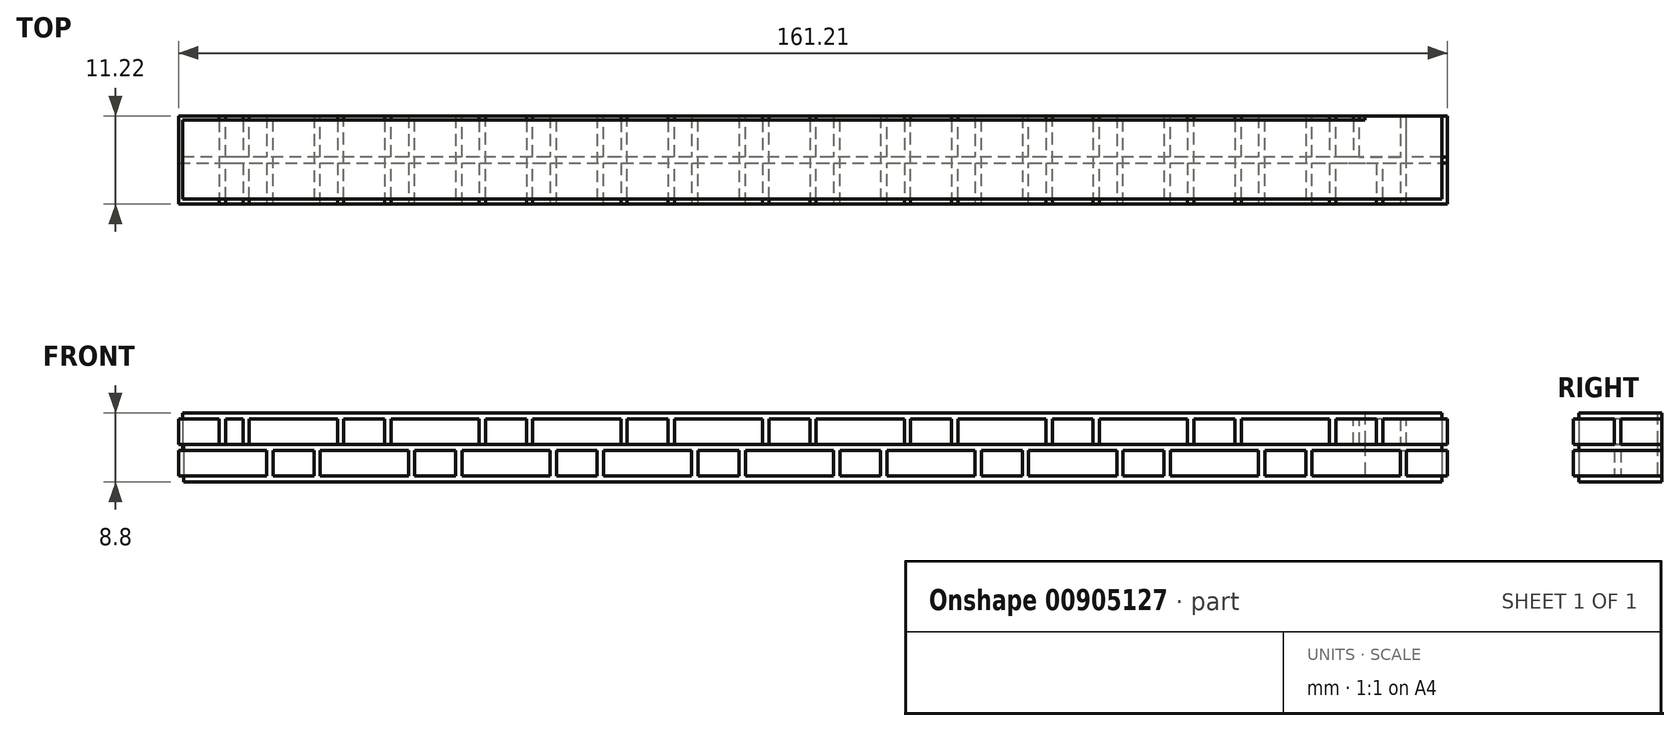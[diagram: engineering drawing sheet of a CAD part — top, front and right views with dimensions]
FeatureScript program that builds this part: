
annotation { "Feature Type Name" : "Feature", "Feature Type Description" : "" }
export const myFeature = defineFeature(function(context is Context, id is Id, definition is map)
    precondition{}
    {
        {
            var Q0;
            Q0=qCreatedBy(makeId("Top.planeOp"),FACE);
            var sketch = newSketch(context, id + "F0", { "sketchPlane" : qUnion([Q0])});
            skLineSegment(sketch, "E0", {"start": v(-80.6, -54.4) * mm, "end": v(-69.4, -54.4) * mm});
            skLineSegment(sketch, "E1", {"start": v(-69.4, -54.4) * mm, "end": v(-69.4, -59.6) * mm});
            skLineSegment(sketch, "E2", {"start": v(-69.4, -59.6) * mm, "end": v(-80.6, -59.6) * mm});
            skLineSegment(sketch, "E3", {"start": v(-80.6, -59.6) * mm, "end": v(-80.6, -54.4) * mm});
            skLineSegment(sketch, "E4", {"start": v(-68.6, -54.4) * mm, "end": v(-63.4, -54.4) * mm});
            skLineSegment(sketch, "E5", {"start": v(-63.4, -54.4) * mm, "end": v(-63.4, -65.6) * mm});
            skLineSegment(sketch, "E6", {"start": v(-63.4, -65.6) * mm, "end": v(-68.6, -65.6) * mm});
            skLineSegment(sketch, "E7", {"start": v(-68.6, -65.6) * mm, "end": v(-68.6, -54.4) * mm});
            skLineSegment(sketch, "E8", {"start": v(-80.6, -60.4) * mm, "end": v(-69.4, -60.4) * mm});
            skLineSegment(sketch, "E9", {"start": v(-69.4, -60.4) * mm, "end": v(-69.4, -65.6) * mm});
            skLineSegment(sketch, "E10", {"start": v(-69.4, -65.6) * mm, "end": v(-80.6, -65.6) * mm});
            skLineSegment(sketch, "E11", {"start": v(-80.6, -65.6) * mm, "end": v(-80.6, -60.4) * mm});
            skLineSegment(sketch, "E12", {"start": v(-62.6, -54.4) * mm, "end": v(-51.4, -54.4) * mm});
            skLineSegment(sketch, "E13", {"start": v(-51.4, -54.4) * mm, "end": v(-51.4, -59.6) * mm});
            skLineSegment(sketch, "E14", {"start": v(-51.4, -59.6) * mm, "end": v(-62.6, -59.6) * mm});
            skLineSegment(sketch, "E15", {"start": v(-62.6, -59.6) * mm, "end": v(-62.6, -54.4) * mm});
            skLineSegment(sketch, "E16", {"start": v(-50.6, -54.4) * mm, "end": v(-45.4, -54.4) * mm});
            skLineSegment(sketch, "E17", {"start": v(-45.4, -54.4) * mm, "end": v(-45.4, -65.6) * mm});
            skLineSegment(sketch, "E18", {"start": v(-45.4, -65.6) * mm, "end": v(-50.6, -65.6) * mm});
            skLineSegment(sketch, "E19", {"start": v(-50.6, -65.6) * mm, "end": v(-50.6, -54.4) * mm});
            skLineSegment(sketch, "E20", {"start": v(-62.6, -60.4) * mm, "end": v(-51.4, -60.4) * mm});
            skLineSegment(sketch, "E21", {"start": v(-51.4, -60.4) * mm, "end": v(-51.4, -65.6) * mm});
            skLineSegment(sketch, "E22", {"start": v(-51.4, -65.6) * mm, "end": v(-62.6, -65.6) * mm});
            skLineSegment(sketch, "E23", {"start": v(-62.6, -65.6) * mm, "end": v(-62.6, -60.4) * mm});
            skLineSegment(sketch, "E24", {"start": v(-44.6, -54.4) * mm, "end": v(-33.4, -54.4) * mm});
            skLineSegment(sketch, "E25", {"start": v(-33.4, -54.4) * mm, "end": v(-33.4, -59.6) * mm});
            skLineSegment(sketch, "E26", {"start": v(-33.4, -59.6) * mm, "end": v(-44.6, -59.6) * mm});
            skLineSegment(sketch, "E27", {"start": v(-44.6, -59.6) * mm, "end": v(-44.6, -54.4) * mm});
            skLineSegment(sketch, "E28", {"start": v(-32.6, -54.4) * mm, "end": v(-27.4, -54.4) * mm});
            skLineSegment(sketch, "E29", {"start": v(-27.4, -54.4) * mm, "end": v(-27.4, -65.6) * mm});
            skLineSegment(sketch, "E30", {"start": v(-27.4, -65.6) * mm, "end": v(-32.6, -65.6) * mm});
            skLineSegment(sketch, "E31", {"start": v(-32.6, -65.6) * mm, "end": v(-32.6, -54.4) * mm});
            skLineSegment(sketch, "E32", {"start": v(-44.6, -60.4) * mm, "end": v(-33.4, -60.4) * mm});
            skLineSegment(sketch, "E33", {"start": v(-33.4, -60.4) * mm, "end": v(-33.4, -65.6) * mm});
            skLineSegment(sketch, "E34", {"start": v(-33.4, -65.6) * mm, "end": v(-44.6, -65.6) * mm});
            skLineSegment(sketch, "E35", {"start": v(-44.6, -65.6) * mm, "end": v(-44.6, -60.4) * mm});
            skLineSegment(sketch, "E36", {"start": v(-26.6, -54.4) * mm, "end": v(-15.4, -54.4) * mm});
            skLineSegment(sketch, "E37", {"start": v(-15.4, -54.4) * mm, "end": v(-15.4, -59.6) * mm});
            skLineSegment(sketch, "E38", {"start": v(-15.4, -59.6) * mm, "end": v(-26.6, -59.6) * mm});
            skLineSegment(sketch, "E39", {"start": v(-26.6, -59.6) * mm, "end": v(-26.6, -54.4) * mm});
            skLineSegment(sketch, "E40", {"start": v(-14.6, -54.4) * mm, "end": v(-9.4, -54.4) * mm});
            skLineSegment(sketch, "E41", {"start": v(-9.4, -54.4) * mm, "end": v(-9.4, -65.6) * mm});
            skLineSegment(sketch, "E42", {"start": v(-9.4, -65.6) * mm, "end": v(-14.6, -65.6) * mm});
            skLineSegment(sketch, "E43", {"start": v(-14.6, -65.6) * mm, "end": v(-14.6, -54.4) * mm});
            skLineSegment(sketch, "E44", {"start": v(-26.6, -60.4) * mm, "end": v(-15.4, -60.4) * mm});
            skLineSegment(sketch, "E45", {"start": v(-15.4, -60.4) * mm, "end": v(-15.4, -65.6) * mm});
            skLineSegment(sketch, "E46", {"start": v(-15.4, -65.6) * mm, "end": v(-26.6, -65.6) * mm});
            skLineSegment(sketch, "E47", {"start": v(-26.6, -65.6) * mm, "end": v(-26.6, -60.4) * mm});
            skLineSegment(sketch, "E48", {"start": v(-8.6, -54.4) * mm, "end": v(2.6, -54.4) * mm});
            skLineSegment(sketch, "E49", {"start": v(2.6, -54.4) * mm, "end": v(2.6, -59.6) * mm});
            skLineSegment(sketch, "E50", {"start": v(2.6, -59.6) * mm, "end": v(-8.6, -59.6) * mm});
            skLineSegment(sketch, "E51", {"start": v(-8.6, -59.6) * mm, "end": v(-8.6, -54.4) * mm});
            skLineSegment(sketch, "E52", {"start": v(3.4, -54.4) * mm, "end": v(8.6, -54.4) * mm});
            skLineSegment(sketch, "E53", {"start": v(8.6, -54.4) * mm, "end": v(8.6, -65.6) * mm});
            skLineSegment(sketch, "E54", {"start": v(8.6, -65.6) * mm, "end": v(3.4, -65.6) * mm});
            skLineSegment(sketch, "E55", {"start": v(3.4, -65.6) * mm, "end": v(3.4, -54.4) * mm});
            skLineSegment(sketch, "E56", {"start": v(-8.6, -60.4) * mm, "end": v(2.6, -60.4) * mm});
            skLineSegment(sketch, "E57", {"start": v(2.6, -60.4) * mm, "end": v(2.6, -65.6) * mm});
            skLineSegment(sketch, "E58", {"start": v(2.6, -65.6) * mm, "end": v(-8.6, -65.6) * mm});
            skLineSegment(sketch, "E59", {"start": v(-8.6, -65.6) * mm, "end": v(-8.6, -60.4) * mm});
            skLineSegment(sketch, "E60", {"start": v(9.4, -54.4) * mm, "end": v(20.6, -54.4) * mm});
            skLineSegment(sketch, "E61", {"start": v(20.6, -54.4) * mm, "end": v(20.6, -59.6) * mm});
            skLineSegment(sketch, "E62", {"start": v(20.6, -59.6) * mm, "end": v(9.4, -59.6) * mm});
            skLineSegment(sketch, "E63", {"start": v(9.4, -59.6) * mm, "end": v(9.4, -54.4) * mm});
            skLineSegment(sketch, "E64", {"start": v(21.4, -54.4) * mm, "end": v(26.6, -54.4) * mm});
            skLineSegment(sketch, "E65", {"start": v(26.6, -54.4) * mm, "end": v(26.6, -65.6) * mm});
            skLineSegment(sketch, "E66", {"start": v(26.6, -65.6) * mm, "end": v(21.4, -65.6) * mm});
            skLineSegment(sketch, "E67", {"start": v(21.4, -65.6) * mm, "end": v(21.4, -54.4) * mm});
            skLineSegment(sketch, "E68", {"start": v(9.4, -60.4) * mm, "end": v(20.6, -60.4) * mm});
            skLineSegment(sketch, "E69", {"start": v(20.6, -60.4) * mm, "end": v(20.6, -65.6) * mm});
            skLineSegment(sketch, "E70", {"start": v(20.6, -65.6) * mm, "end": v(9.4, -65.6) * mm});
            skLineSegment(sketch, "E71", {"start": v(9.4, -65.6) * mm, "end": v(9.4, -60.4) * mm});
            skLineSegment(sketch, "E72", {"start": v(27.4, -54.4) * mm, "end": v(38.6, -54.4) * mm});
            skLineSegment(sketch, "E73", {"start": v(38.6, -54.4) * mm, "end": v(38.6, -59.6) * mm});
            skLineSegment(sketch, "E74", {"start": v(38.6, -59.6) * mm, "end": v(27.4, -59.6) * mm});
            skLineSegment(sketch, "E75", {"start": v(27.4, -59.6) * mm, "end": v(27.4, -54.4) * mm});
            skLineSegment(sketch, "E76", {"start": v(39.4, -54.4) * mm, "end": v(44.6, -54.4) * mm});
            skLineSegment(sketch, "E77", {"start": v(44.6, -54.4) * mm, "end": v(44.6, -65.6) * mm});
            skLineSegment(sketch, "E78", {"start": v(44.6, -65.6) * mm, "end": v(39.4, -65.6) * mm});
            skLineSegment(sketch, "E79", {"start": v(39.4, -65.6) * mm, "end": v(39.4, -54.4) * mm});
            skLineSegment(sketch, "E80", {"start": v(27.4, -60.4) * mm, "end": v(38.6, -60.4) * mm});
            skLineSegment(sketch, "E81", {"start": v(38.6, -60.4) * mm, "end": v(38.6, -65.6) * mm});
            skLineSegment(sketch, "E82", {"start": v(38.6, -65.6) * mm, "end": v(27.4, -65.6) * mm});
            skLineSegment(sketch, "E83", {"start": v(27.4, -65.6) * mm, "end": v(27.4, -60.4) * mm});
            skLineSegment(sketch, "E84", {"start": v(45.4, -54.4) * mm, "end": v(56.6, -54.4) * mm});
            skLineSegment(sketch, "E85", {"start": v(56.6, -54.4) * mm, "end": v(56.6, -59.6) * mm});
            skLineSegment(sketch, "E86", {"start": v(56.6, -59.6) * mm, "end": v(45.4, -59.6) * mm});
            skLineSegment(sketch, "E87", {"start": v(45.4, -59.6) * mm, "end": v(45.4, -54.4) * mm});
            skLineSegment(sketch, "E88", {"start": v(57.4, -54.4) * mm, "end": v(62.6, -54.4) * mm});
            skLineSegment(sketch, "E89", {"start": v(62.6, -54.4) * mm, "end": v(62.6, -65.6) * mm});
            skLineSegment(sketch, "E90", {"start": v(62.6, -65.6) * mm, "end": v(57.4, -65.6) * mm});
            skLineSegment(sketch, "E91", {"start": v(57.4, -65.6) * mm, "end": v(57.4, -54.4) * mm});
            skLineSegment(sketch, "E92", {"start": v(45.4, -60.4) * mm, "end": v(56.6, -60.4) * mm});
            skLineSegment(sketch, "E93", {"start": v(56.6, -60.4) * mm, "end": v(56.6, -65.6) * mm});
            skLineSegment(sketch, "E94", {"start": v(56.6, -65.6) * mm, "end": v(45.4, -65.6) * mm});
            skLineSegment(sketch, "E95", {"start": v(45.4, -65.6) * mm, "end": v(45.4, -60.4) * mm});
            skLineSegment(sketch, "E96", {"start": v(63.4, -54.4) * mm, "end": v(74.6, -54.4) * mm});
            skLineSegment(sketch, "E97", {"start": v(74.6, -54.4) * mm, "end": v(74.6, -59.6) * mm});
            skLineSegment(sketch, "E98", {"start": v(74.6, -59.6) * mm, "end": v(63.4, -59.6) * mm});
            skLineSegment(sketch, "E99", {"start": v(63.4, -59.6) * mm, "end": v(63.4, -54.4) * mm});
            skLineSegment(sketch, "E100", {"start": v(75.4, -54.4) * mm, "end": v(80.6, -54.4) * mm});
            skLineSegment(sketch, "E101", {"start": v(80.6, -54.4) * mm, "end": v(80.6, -65.6) * mm});
            skLineSegment(sketch, "E102", {"start": v(80.6, -65.6) * mm, "end": v(75.4, -65.6) * mm});
            skLineSegment(sketch, "E103", {"start": v(75.4, -65.6) * mm, "end": v(75.4, -54.4) * mm});
            skLineSegment(sketch, "E104", {"start": v(63.4, -60.4) * mm, "end": v(74.6, -60.4) * mm});
            skLineSegment(sketch, "E105", {"start": v(74.6, -60.4) * mm, "end": v(74.6, -65.6) * mm});
            skLineSegment(sketch, "E106", {"start": v(74.6, -65.6) * mm, "end": v(63.4, -65.6) * mm});
            skLineSegment(sketch, "E107", {"start": v(63.4, -65.6) * mm, "end": v(63.4, -60.4) * mm});
            skLineSegment(sketch, "E108", {"start": v(69.4, -53.6) * mm, "end": v(69.4, -42.4) * mm});
            skLineSegment(sketch, "E109", {"start": v(69.4, -42.4) * mm, "end": v(74.6, -42.4) * mm});
            skLineSegment(sketch, "E110", {"start": v(74.6, -42.4) * mm, "end": v(74.6, -53.6) * mm});
            skLineSegment(sketch, "E111", {"start": v(74.6, -53.6) * mm, "end": v(69.4, -53.6) * mm});
            skLineSegment(sketch, "E112", {"start": v(69.4, -41.6) * mm, "end": v(69.4, -36.4) * mm});
            skLineSegment(sketch, "E113", {"start": v(69.4, -36.4) * mm, "end": v(80.6, -36.4) * mm});
            skLineSegment(sketch, "E114", {"start": v(80.6, -36.4) * mm, "end": v(80.6, -41.6) * mm});
            skLineSegment(sketch, "E115", {"start": v(80.6, -41.6) * mm, "end": v(69.4, -41.6) * mm});
            skLineSegment(sketch, "E116", {"start": v(75.4, -53.6) * mm, "end": v(75.4, -42.4) * mm});
            skLineSegment(sketch, "E117", {"start": v(75.4, -42.4) * mm, "end": v(80.6, -42.4) * mm});
            skLineSegment(sketch, "E118", {"start": v(80.6, -42.4) * mm, "end": v(80.6, -53.6) * mm});
            skLineSegment(sketch, "E119", {"start": v(80.6, -53.6) * mm, "end": v(75.4, -53.6) * mm});
            skLineSegment(sketch, "E120", {"start": v(69.4, -35.6) * mm, "end": v(69.4, -24.4) * mm});
            skLineSegment(sketch, "E121", {"start": v(69.4, -24.4) * mm, "end": v(74.6, -24.4) * mm});
            skLineSegment(sketch, "E122", {"start": v(74.6, -24.4) * mm, "end": v(74.6, -35.6) * mm});
            skLineSegment(sketch, "E123", {"start": v(74.6, -35.6) * mm, "end": v(69.4, -35.6) * mm});
            skLineSegment(sketch, "E124", {"start": v(69.4, -23.6) * mm, "end": v(69.4, -18.4) * mm});
            skLineSegment(sketch, "E125", {"start": v(69.4, -18.4) * mm, "end": v(80.6, -18.4) * mm});
            skLineSegment(sketch, "E126", {"start": v(80.6, -18.4) * mm, "end": v(80.6, -23.6) * mm});
            skLineSegment(sketch, "E127", {"start": v(80.6, -23.6) * mm, "end": v(69.4, -23.6) * mm});
            skLineSegment(sketch, "E128", {"start": v(75.4, -35.6) * mm, "end": v(75.4, -24.4) * mm});
            skLineSegment(sketch, "E129", {"start": v(75.4, -24.4) * mm, "end": v(80.6, -24.4) * mm});
            skLineSegment(sketch, "E130", {"start": v(80.6, -24.4) * mm, "end": v(80.6, -35.6) * mm});
            skLineSegment(sketch, "E131", {"start": v(80.6, -35.6) * mm, "end": v(75.4, -35.6) * mm});
            skLineSegment(sketch, "E132", {"start": v(69.4, -17.6) * mm, "end": v(69.4, -6.4) * mm});
            skLineSegment(sketch, "E133", {"start": v(69.4, -6.4) * mm, "end": v(74.6, -6.4) * mm});
            skLineSegment(sketch, "E134", {"start": v(74.6, -6.4) * mm, "end": v(74.6, -17.6) * mm});
            skLineSegment(sketch, "E135", {"start": v(74.6, -17.6) * mm, "end": v(69.4, -17.6) * mm});
            skLineSegment(sketch, "E136", {"start": v(69.4, -5.6) * mm, "end": v(69.4, -0.4) * mm});
            skLineSegment(sketch, "E137", {"start": v(69.4, -0.4) * mm, "end": v(80.6, -0.4) * mm});
            skLineSegment(sketch, "E138", {"start": v(80.6, -0.4) * mm, "end": v(80.6, -5.6) * mm});
            skLineSegment(sketch, "E139", {"start": v(80.6, -5.6) * mm, "end": v(69.4, -5.6) * mm});
            skLineSegment(sketch, "E140", {"start": v(75.4, -17.6) * mm, "end": v(75.4, -6.4) * mm});
            skLineSegment(sketch, "E141", {"start": v(75.4, -6.4) * mm, "end": v(80.6, -6.4) * mm});
            skLineSegment(sketch, "E142", {"start": v(80.6, -6.4) * mm, "end": v(80.6, -17.6) * mm});
            skLineSegment(sketch, "E143", {"start": v(80.6, -17.6) * mm, "end": v(75.4, -17.6) * mm});
            skLineSegment(sketch, "E144", {"start": v(69.4, 0.4) * mm, "end": v(69.4, 11.6) * mm});
            skLineSegment(sketch, "E145", {"start": v(69.4, 11.6) * mm, "end": v(74.6, 11.6) * mm});
            skLineSegment(sketch, "E146", {"start": v(74.6, 11.6) * mm, "end": v(74.6, 0.4) * mm});
            skLineSegment(sketch, "E147", {"start": v(74.6, 0.4) * mm, "end": v(69.4, 0.4) * mm});
            skLineSegment(sketch, "E148", {"start": v(69.4, 12.4) * mm, "end": v(69.4, 17.6) * mm});
            skLineSegment(sketch, "E149", {"start": v(69.4, 17.6) * mm, "end": v(80.6, 17.6) * mm});
            skLineSegment(sketch, "E150", {"start": v(80.6, 17.6) * mm, "end": v(80.6, 12.4) * mm});
            skLineSegment(sketch, "E151", {"start": v(80.6, 12.4) * mm, "end": v(69.4, 12.4) * mm});
            skLineSegment(sketch, "E152", {"start": v(75.4, 0.4) * mm, "end": v(75.4, 11.6) * mm});
            skLineSegment(sketch, "E153", {"start": v(75.4, 11.6) * mm, "end": v(80.6, 11.6) * mm});
            skLineSegment(sketch, "E154", {"start": v(80.6, 11.6) * mm, "end": v(80.6, 0.4) * mm});
            skLineSegment(sketch, "E155", {"start": v(80.6, 0.4) * mm, "end": v(75.4, 0.4) * mm});
            skLineSegment(sketch, "E156", {"start": v(69.4, 18.4) * mm, "end": v(69.4, 29.6) * mm});
            skLineSegment(sketch, "E157", {"start": v(69.4, 29.6) * mm, "end": v(74.6, 29.6) * mm});
            skLineSegment(sketch, "E158", {"start": v(74.6, 29.6) * mm, "end": v(74.6, 18.4) * mm});
            skLineSegment(sketch, "E159", {"start": v(74.6, 18.4) * mm, "end": v(69.4, 18.4) * mm});
            skLineSegment(sketch, "E160", {"start": v(69.4, 30.4) * mm, "end": v(69.4, 35.6) * mm});
            skLineSegment(sketch, "E161", {"start": v(69.4, 35.6) * mm, "end": v(80.6, 35.6) * mm});
            skLineSegment(sketch, "E162", {"start": v(80.6, 35.6) * mm, "end": v(80.6, 30.4) * mm});
            skLineSegment(sketch, "E163", {"start": v(80.6, 30.4) * mm, "end": v(69.4, 30.4) * mm});
            skLineSegment(sketch, "E164", {"start": v(75.4, 18.4) * mm, "end": v(75.4, 29.6) * mm});
            skLineSegment(sketch, "E165", {"start": v(75.4, 29.6) * mm, "end": v(80.6, 29.6) * mm});
            skLineSegment(sketch, "E166", {"start": v(80.6, 29.6) * mm, "end": v(80.6, 18.4) * mm});
            skLineSegment(sketch, "E167", {"start": v(80.6, 18.4) * mm, "end": v(75.4, 18.4) * mm});
            skLineSegment(sketch, "E168", {"start": v(69.4, 36.4) * mm, "end": v(69.4, 47.6) * mm});
            skLineSegment(sketch, "E169", {"start": v(69.4, 47.6) * mm, "end": v(74.6, 47.6) * mm});
            skLineSegment(sketch, "E170", {"start": v(74.6, 47.6) * mm, "end": v(74.6, 36.4) * mm});
            skLineSegment(sketch, "E171", {"start": v(74.6, 36.4) * mm, "end": v(69.4, 36.4) * mm});
            skLineSegment(sketch, "E172", {"start": v(69.4, 48.4) * mm, "end": v(69.4, 53.6) * mm});
            skLineSegment(sketch, "E173", {"start": v(69.4, 53.6) * mm, "end": v(80.6, 53.6) * mm});
            skLineSegment(sketch, "E174", {"start": v(80.6, 53.6) * mm, "end": v(80.6, 48.4) * mm});
            skLineSegment(sketch, "E175", {"start": v(80.6, 48.4) * mm, "end": v(69.4, 48.4) * mm});
            skLineSegment(sketch, "E176", {"start": v(75.4, 36.4) * mm, "end": v(75.4, 47.6) * mm});
            skLineSegment(sketch, "E177", {"start": v(75.4, 47.6) * mm, "end": v(80.6, 47.6) * mm});
            skLineSegment(sketch, "E178", {"start": v(80.6, 47.6) * mm, "end": v(80.6, 36.4) * mm});
            skLineSegment(sketch, "E179", {"start": v(80.6, 36.4) * mm, "end": v(75.4, 36.4) * mm});
            skLineSegment(sketch, "E180", {"start": v(75.4, 54.4) * mm, "end": v(75.4, 65.6) * mm});
            skLineSegment(sketch, "E181", {"start": v(75.4, 65.6) * mm, "end": v(80.6, 65.6) * mm});
            skLineSegment(sketch, "E182", {"start": v(80.6, 65.6) * mm, "end": v(80.6, 54.4) * mm});
            skLineSegment(sketch, "E183", {"start": v(80.6, 54.4) * mm, "end": v(75.4, 54.4) * mm});
            skLineSegment(sketch, "E184", {"start": v(-80.6, 65.6) * mm, "end": v(-69.4, 65.6) * mm});
            skLineSegment(sketch, "E185", {"start": v(-69.4, 65.6) * mm, "end": v(-69.4, 60.4) * mm});
            skLineSegment(sketch, "E186", {"start": v(-69.4, 60.4) * mm, "end": v(-80.6, 60.4) * mm});
            skLineSegment(sketch, "E187", {"start": v(-80.6, 60.4) * mm, "end": v(-80.6, 65.6) * mm});
            skLineSegment(sketch, "E188", {"start": v(-68.6, 65.6) * mm, "end": v(-63.4, 65.6) * mm});
            skLineSegment(sketch, "E189", {"start": v(-63.4, 65.6) * mm, "end": v(-63.4, 54.4) * mm});
            skLineSegment(sketch, "E190", {"start": v(-63.4, 54.4) * mm, "end": v(-68.6, 54.4) * mm});
            skLineSegment(sketch, "E191", {"start": v(-68.6, 54.4) * mm, "end": v(-68.6, 65.6) * mm});
            skLineSegment(sketch, "E192", {"start": v(-80.6, 59.6) * mm, "end": v(-69.4, 59.6) * mm});
            skLineSegment(sketch, "E193", {"start": v(-69.4, 59.6) * mm, "end": v(-69.4, 54.4) * mm});
            skLineSegment(sketch, "E194", {"start": v(-69.4, 54.4) * mm, "end": v(-80.6, 54.4) * mm});
            skLineSegment(sketch, "E195", {"start": v(-80.6, 54.4) * mm, "end": v(-80.6, 59.6) * mm});
            skLineSegment(sketch, "E196", {"start": v(-62.6, 65.6) * mm, "end": v(-51.4, 65.6) * mm});
            skLineSegment(sketch, "E197", {"start": v(-51.4, 65.6) * mm, "end": v(-51.4, 60.4) * mm});
            skLineSegment(sketch, "E198", {"start": v(-51.4, 60.4) * mm, "end": v(-62.6, 60.4) * mm});
            skLineSegment(sketch, "E199", {"start": v(-62.6, 60.4) * mm, "end": v(-62.6, 65.6) * mm});
            skLineSegment(sketch, "E200", {"start": v(-50.6, 65.6) * mm, "end": v(-45.4, 65.6) * mm});
            skLineSegment(sketch, "E201", {"start": v(-45.4, 65.6) * mm, "end": v(-45.4, 54.4) * mm});
            skLineSegment(sketch, "E202", {"start": v(-45.4, 54.4) * mm, "end": v(-50.6, 54.4) * mm});
            skLineSegment(sketch, "E203", {"start": v(-50.6, 54.4) * mm, "end": v(-50.6, 65.6) * mm});
            skLineSegment(sketch, "E204", {"start": v(-62.6, 59.6) * mm, "end": v(-51.4, 59.6) * mm});
            skLineSegment(sketch, "E205", {"start": v(-51.4, 59.6) * mm, "end": v(-51.4, 54.4) * mm});
            skLineSegment(sketch, "E206", {"start": v(-51.4, 54.4) * mm, "end": v(-62.6, 54.4) * mm});
            skLineSegment(sketch, "E207", {"start": v(-62.6, 54.4) * mm, "end": v(-62.6, 59.6) * mm});
            skLineSegment(sketch, "E208", {"start": v(-44.6, 65.6) * mm, "end": v(-33.4, 65.6) * mm});
            skLineSegment(sketch, "E209", {"start": v(-33.4, 65.6) * mm, "end": v(-33.4, 60.4) * mm});
            skLineSegment(sketch, "E210", {"start": v(-33.4, 60.4) * mm, "end": v(-44.6, 60.4) * mm});
            skLineSegment(sketch, "E211", {"start": v(-44.6, 60.4) * mm, "end": v(-44.6, 65.6) * mm});
            skLineSegment(sketch, "E212", {"start": v(-32.6, 65.6) * mm, "end": v(-27.4, 65.6) * mm});
            skLineSegment(sketch, "E213", {"start": v(-27.4, 65.6) * mm, "end": v(-27.4, 54.4) * mm});
            skLineSegment(sketch, "E214", {"start": v(-27.4, 54.4) * mm, "end": v(-32.6, 54.4) * mm});
            skLineSegment(sketch, "E215", {"start": v(-32.6, 54.4) * mm, "end": v(-32.6, 65.6) * mm});
            skLineSegment(sketch, "E216", {"start": v(-44.6, 59.6) * mm, "end": v(-33.4, 59.6) * mm});
            skLineSegment(sketch, "E217", {"start": v(-33.4, 59.6) * mm, "end": v(-33.4, 54.4) * mm});
            skLineSegment(sketch, "E218", {"start": v(-33.4, 54.4) * mm, "end": v(-44.6, 54.4) * mm});
            skLineSegment(sketch, "E219", {"start": v(-44.6, 54.4) * mm, "end": v(-44.6, 59.6) * mm});
            skLineSegment(sketch, "E220", {"start": v(-26.6, 65.6) * mm, "end": v(-15.4, 65.6) * mm});
            skLineSegment(sketch, "E221", {"start": v(-15.4, 65.6) * mm, "end": v(-15.4, 60.4) * mm});
            skLineSegment(sketch, "E222", {"start": v(-15.4, 60.4) * mm, "end": v(-26.6, 60.4) * mm});
            skLineSegment(sketch, "E223", {"start": v(-26.6, 60.4) * mm, "end": v(-26.6, 65.6) * mm});
            skLineSegment(sketch, "E224", {"start": v(-14.6, 65.6) * mm, "end": v(-9.4, 65.6) * mm});
            skLineSegment(sketch, "E225", {"start": v(-9.4, 65.6) * mm, "end": v(-9.4, 54.4) * mm});
            skLineSegment(sketch, "E226", {"start": v(-9.4, 54.4) * mm, "end": v(-14.6, 54.4) * mm});
            skLineSegment(sketch, "E227", {"start": v(-14.6, 54.4) * mm, "end": v(-14.6, 65.6) * mm});
            skLineSegment(sketch, "E228", {"start": v(-26.6, 59.6) * mm, "end": v(-15.4, 59.6) * mm});
            skLineSegment(sketch, "E229", {"start": v(-15.4, 59.6) * mm, "end": v(-15.4, 54.4) * mm});
            skLineSegment(sketch, "E230", {"start": v(-15.4, 54.4) * mm, "end": v(-26.6, 54.4) * mm});
            skLineSegment(sketch, "E231", {"start": v(-26.6, 54.4) * mm, "end": v(-26.6, 59.6) * mm});
            skLineSegment(sketch, "E232", {"start": v(-8.6, 65.6) * mm, "end": v(2.6, 65.6) * mm});
            skLineSegment(sketch, "E233", {"start": v(2.6, 65.6) * mm, "end": v(2.6, 60.4) * mm});
            skLineSegment(sketch, "E234", {"start": v(2.6, 60.4) * mm, "end": v(-8.6, 60.4) * mm});
            skLineSegment(sketch, "E235", {"start": v(-8.6, 60.4) * mm, "end": v(-8.6, 65.6) * mm});
            skLineSegment(sketch, "E236", {"start": v(3.4, 65.6) * mm, "end": v(8.6, 65.6) * mm});
            skLineSegment(sketch, "E237", {"start": v(8.6, 65.6) * mm, "end": v(8.6, 54.4) * mm});
            skLineSegment(sketch, "E238", {"start": v(8.6, 54.4) * mm, "end": v(3.4, 54.4) * mm});
            skLineSegment(sketch, "E239", {"start": v(3.4, 54.4) * mm, "end": v(3.4, 65.6) * mm});
            skLineSegment(sketch, "E240", {"start": v(-8.6, 59.6) * mm, "end": v(2.6, 59.6) * mm});
            skLineSegment(sketch, "E241", {"start": v(2.6, 59.6) * mm, "end": v(2.6, 54.4) * mm});
            skLineSegment(sketch, "E242", {"start": v(2.6, 54.4) * mm, "end": v(-8.6, 54.4) * mm});
            skLineSegment(sketch, "E243", {"start": v(-8.6, 54.4) * mm, "end": v(-8.6, 59.6) * mm});
            skLineSegment(sketch, "E244", {"start": v(9.4, 65.6) * mm, "end": v(20.6, 65.6) * mm});
            skLineSegment(sketch, "E245", {"start": v(20.6, 65.6) * mm, "end": v(20.6, 60.4) * mm});
            skLineSegment(sketch, "E246", {"start": v(20.6, 60.4) * mm, "end": v(9.4, 60.4) * mm});
            skLineSegment(sketch, "E247", {"start": v(9.4, 60.4) * mm, "end": v(9.4, 65.6) * mm});
            skLineSegment(sketch, "E248", {"start": v(21.4, 65.6) * mm, "end": v(26.6, 65.6) * mm});
            skLineSegment(sketch, "E249", {"start": v(26.6, 65.6) * mm, "end": v(26.6, 54.4) * mm});
            skLineSegment(sketch, "E250", {"start": v(26.6, 54.4) * mm, "end": v(21.4, 54.4) * mm});
            skLineSegment(sketch, "E251", {"start": v(21.4, 54.4) * mm, "end": v(21.4, 65.6) * mm});
            skLineSegment(sketch, "E252", {"start": v(9.4, 59.6) * mm, "end": v(20.6, 59.6) * mm});
            skLineSegment(sketch, "E253", {"start": v(20.6, 59.6) * mm, "end": v(20.6, 54.4) * mm});
            skLineSegment(sketch, "E254", {"start": v(20.6, 54.4) * mm, "end": v(9.4, 54.4) * mm});
            skLineSegment(sketch, "E255", {"start": v(9.4, 54.4) * mm, "end": v(9.4, 59.6) * mm});
            skLineSegment(sketch, "E256", {"start": v(27.4, 65.6) * mm, "end": v(38.6, 65.6) * mm});
            skLineSegment(sketch, "E257", {"start": v(38.6, 65.6) * mm, "end": v(38.6, 60.4) * mm});
            skLineSegment(sketch, "E258", {"start": v(38.6, 60.4) * mm, "end": v(27.4, 60.4) * mm});
            skLineSegment(sketch, "E259", {"start": v(27.4, 60.4) * mm, "end": v(27.4, 65.6) * mm});
            skLineSegment(sketch, "E260", {"start": v(39.4, 65.6) * mm, "end": v(44.6, 65.6) * mm});
            skLineSegment(sketch, "E261", {"start": v(44.6, 65.6) * mm, "end": v(44.6, 54.4) * mm});
            skLineSegment(sketch, "E262", {"start": v(44.6, 54.4) * mm, "end": v(39.4, 54.4) * mm});
            skLineSegment(sketch, "E263", {"start": v(39.4, 54.4) * mm, "end": v(39.4, 65.6) * mm});
            skLineSegment(sketch, "E264", {"start": v(27.4, 59.6) * mm, "end": v(38.6, 59.6) * mm});
            skLineSegment(sketch, "E265", {"start": v(38.6, 59.6) * mm, "end": v(38.6, 54.4) * mm});
            skLineSegment(sketch, "E266", {"start": v(38.6, 54.4) * mm, "end": v(27.4, 54.4) * mm});
            skLineSegment(sketch, "E267", {"start": v(27.4, 54.4) * mm, "end": v(27.4, 59.6) * mm});
            skLineSegment(sketch, "E268", {"start": v(45.4, 65.6) * mm, "end": v(56.6, 65.6) * mm});
            skLineSegment(sketch, "E269", {"start": v(56.6, 65.6) * mm, "end": v(56.6, 60.4) * mm});
            skLineSegment(sketch, "E270", {"start": v(56.6, 60.4) * mm, "end": v(45.4, 60.4) * mm});
            skLineSegment(sketch, "E271", {"start": v(45.4, 60.4) * mm, "end": v(45.4, 65.6) * mm});
            skLineSegment(sketch, "E272", {"start": v(57.4, 65.6) * mm, "end": v(62.6, 65.6) * mm});
            skLineSegment(sketch, "E273", {"start": v(62.6, 65.6) * mm, "end": v(62.6, 54.4) * mm});
            skLineSegment(sketch, "E274", {"start": v(62.6, 54.4) * mm, "end": v(57.4, 54.4) * mm});
            skLineSegment(sketch, "E275", {"start": v(57.4, 54.4) * mm, "end": v(57.4, 65.6) * mm});
            skLineSegment(sketch, "E276", {"start": v(45.4, 59.6) * mm, "end": v(56.6, 59.6) * mm});
            skLineSegment(sketch, "E277", {"start": v(56.6, 59.6) * mm, "end": v(56.6, 54.4) * mm});
            skLineSegment(sketch, "E278", {"start": v(56.6, 54.4) * mm, "end": v(45.4, 54.4) * mm});
            skLineSegment(sketch, "E279", {"start": v(45.4, 54.4) * mm, "end": v(45.4, 59.6) * mm});
            skLineSegment(sketch, "E280", {"start": v(63.4, 65.6) * mm, "end": v(74.6, 65.6) * mm});
            skLineSegment(sketch, "E281", {"start": v(74.6, 65.6) * mm, "end": v(74.6, 60.4) * mm});
            skLineSegment(sketch, "E282", {"start": v(74.6, 60.4) * mm, "end": v(63.4, 60.4) * mm});
            skLineSegment(sketch, "E283", {"start": v(63.4, 60.4) * mm, "end": v(63.4, 65.6) * mm});
            skLineSegment(sketch, "E284", {"start": v(63.4, 59.6) * mm, "end": v(74.6, 59.6) * mm});
            skLineSegment(sketch, "E285", {"start": v(74.6, 59.6) * mm, "end": v(74.6, 54.4) * mm});
            skLineSegment(sketch, "E286", {"start": v(74.6, 54.4) * mm, "end": v(63.4, 54.4) * mm});
            skLineSegment(sketch, "E287", {"start": v(63.4, 54.4) * mm, "end": v(63.4, 59.6) * mm});
            skSolve(sketch);
        }
        {
            var Q0;
            Q0=makeQuery(id+"F0.imprint","IMPRINT",FACE,{"disambiguationData":[TD([[makeQuery(id+"F0.imprint","IMPRINT",EDGE,{"derivedFrom":sQuery(id+"F0.wireOp",EDGE,"E244")}),-1.0]])]});
            var Q1;
            Q1=makeQuery(id+"F0.imprint","IMPRINT",FACE,{"disambiguationData":[TD([[makeQuery(id+"F0.imprint","IMPRINT",EDGE,{"derivedFrom":sQuery(id+"F0.wireOp",EDGE,"E180")}),-1.0]])]});
            var Q2;
            Q2=makeQuery(id+"F0.imprint","IMPRINT",FACE,{"disambiguationData":[TD([[makeQuery(id+"F0.imprint","IMPRINT",EDGE,{"derivedFrom":sQuery(id+"F0.wireOp",EDGE,"E204")}),-1.0]])]});
            var Q3;
            Q3=makeQuery(id+"F0.imprint","IMPRINT",FACE,{"disambiguationData":[TD([[makeQuery(id+"F0.imprint","IMPRINT",EDGE,{"derivedFrom":sQuery(id+"F0.wireOp",EDGE,"E140")}),-1.0]])]});
            var Q4;
            Q4=makeQuery(id+"F0.imprint","IMPRINT",FACE,{"disambiguationData":[TD([[makeQuery(id+"F0.imprint","IMPRINT",EDGE,{"derivedFrom":sQuery(id+"F0.wireOp",EDGE,"E164")}),-1.0]])]});
            var Q5;
            Q5=makeQuery(id+"F0.imprint","IMPRINT",FACE,{"disambiguationData":[TD([[makeQuery(id+"F0.imprint","IMPRINT",EDGE,{"derivedFrom":sQuery(id+"F0.wireOp",EDGE,"E168")}),-1.0]])]});
            var Q6;
            Q6=makeQuery(id+"F0.imprint","IMPRINT",FACE,{"disambiguationData":[TD([[makeQuery(id+"F0.imprint","IMPRINT",EDGE,{"derivedFrom":sQuery(id+"F0.wireOp",EDGE,"E176")}),-1.0]])]});
            var Q7;
            Q7=makeQuery(id+"F0.imprint","IMPRINT",FACE,{"disambiguationData":[TD([[makeQuery(id+"F0.imprint","IMPRINT",EDGE,{"derivedFrom":sQuery(id+"F0.wireOp",EDGE,"E156")}),-1.0]])]});
            var Q8;
            Q8=makeQuery(id+"F0.imprint","IMPRINT",FACE,{"disambiguationData":[TD([[makeQuery(id+"F0.imprint","IMPRINT",EDGE,{"derivedFrom":sQuery(id+"F0.wireOp",EDGE,"E32")}),-1.0]])]});
            var Q9;
            Q9=makeQuery(id+"F0.imprint","IMPRINT",FACE,{"disambiguationData":[TD([[makeQuery(id+"F0.imprint","IMPRINT",EDGE,{"derivedFrom":sQuery(id+"F0.wireOp",EDGE,"E220")}),-1.0]])]});
            var Q10;
            Q10=makeQuery(id+"F0.imprint","IMPRINT",FACE,{"disambiguationData":[TD([[makeQuery(id+"F0.imprint","IMPRINT",EDGE,{"derivedFrom":sQuery(id+"F0.wireOp",EDGE,"E60")}),-1.0]])]});
            var Q11;
            Q11=makeQuery(id+"F0.imprint","IMPRINT",FACE,{"disambiguationData":[TD([[makeQuery(id+"F0.imprint","IMPRINT",EDGE,{"derivedFrom":sQuery(id+"F0.wireOp",EDGE,"E152")}),-1.0]])]});
            var Q12;
            Q12=makeQuery(id+"F0.imprint","IMPRINT",FACE,{"disambiguationData":[TD([[makeQuery(id+"F0.imprint","IMPRINT",EDGE,{"derivedFrom":sQuery(id+"F0.wireOp",EDGE,"E252")}),-1.0]])]});
            var Q13;
            Q13=makeQuery(id+"F0.imprint","IMPRINT",FACE,{"disambiguationData":[TD([[makeQuery(id+"F0.imprint","IMPRINT",EDGE,{"derivedFrom":sQuery(id+"F0.wireOp",EDGE,"E280")}),-1.0]])]});
            var Q14;
            Q14=makeQuery(id+"F0.imprint","IMPRINT",FACE,{"disambiguationData":[TD([[makeQuery(id+"F0.imprint","IMPRINT",EDGE,{"derivedFrom":sQuery(id+"F0.wireOp",EDGE,"E44")}),-1.0]])]});
            var Q15;
            Q15=makeQuery(id+"F0.imprint","IMPRINT",FACE,{"disambiguationData":[TD([[makeQuery(id+"F0.imprint","IMPRINT",EDGE,{"derivedFrom":sQuery(id+"F0.wireOp",EDGE,"E128")}),-1.0]])]});
            var Q16;
            Q16=makeQuery(id+"F0.imprint","IMPRINT",FACE,{"disambiguationData":[TD([[makeQuery(id+"F0.imprint","IMPRINT",EDGE,{"derivedFrom":sQuery(id+"F0.wireOp",EDGE,"E216")}),-1.0]])]});
            var Q17;
            Q17=makeQuery(id+"F0.imprint","IMPRINT",FACE,{"disambiguationData":[TD([[makeQuery(id+"F0.imprint","IMPRINT",EDGE,{"derivedFrom":sQuery(id+"F0.wireOp",EDGE,"E284")}),-1.0]])]});
            var Q18;
            Q18=makeQuery(id+"F0.imprint","IMPRINT",FACE,{"disambiguationData":[TD([[makeQuery(id+"F0.imprint","IMPRINT",EDGE,{"derivedFrom":sQuery(id+"F0.wireOp",EDGE,"E268")}),-1.0]])]});
            var Q19;
            Q19=makeQuery(id+"F0.imprint","IMPRINT",FACE,{"disambiguationData":[TD([[makeQuery(id+"F0.imprint","IMPRINT",EDGE,{"derivedFrom":sQuery(id+"F0.wireOp",EDGE,"E208")}),-1.0]])]});
            var Q20;
            Q20=makeQuery(id+"F0.imprint","IMPRINT",FACE,{"disambiguationData":[TD([[makeQuery(id+"F0.imprint","IMPRINT",EDGE,{"derivedFrom":sQuery(id+"F0.wireOp",EDGE,"E8")}),-1.0]])]});
            var Q21;
            Q21=makeQuery(id+"F0.imprint","IMPRINT",FACE,{"disambiguationData":[TD([[makeQuery(id+"F0.imprint","IMPRINT",EDGE,{"derivedFrom":sQuery(id+"F0.wireOp",EDGE,"E104")}),-1.0]])]});
            var Q22;
            Q22=makeQuery(id+"F0.imprint","IMPRINT",FACE,{"disambiguationData":[TD([[makeQuery(id+"F0.imprint","IMPRINT",EDGE,{"derivedFrom":sQuery(id+"F0.wireOp",EDGE,"E196")}),-1.0]])]});
            var Q23;
            Q23=makeQuery(id+"F0.imprint","IMPRINT",FACE,{"disambiguationData":[TD([[makeQuery(id+"F0.imprint","IMPRINT",EDGE,{"derivedFrom":sQuery(id+"F0.wireOp",EDGE,"E232")}),-1.0]])]});
            var Q24;
            Q24=makeQuery(id+"F0.imprint","IMPRINT",FACE,{"disambiguationData":[TD([[makeQuery(id+"F0.imprint","IMPRINT",EDGE,{"derivedFrom":sQuery(id+"F0.wireOp",EDGE,"E92")}),-1.0]])]});
            var Q25;
            Q25=makeQuery(id+"F0.imprint","IMPRINT",FACE,{"disambiguationData":[TD([[makeQuery(id+"F0.imprint","IMPRINT",EDGE,{"derivedFrom":sQuery(id+"F0.wireOp",EDGE,"E24")}),-1.0]])]});
            var Q26;
            Q26=makeQuery(id+"F0.imprint","IMPRINT",FACE,{"disambiguationData":[TD([[makeQuery(id+"F0.imprint","IMPRINT",EDGE,{"derivedFrom":sQuery(id+"F0.wireOp",EDGE,"E228")}),-1.0]])]});
            var Q27;
            Q27=makeQuery(id+"F0.imprint","IMPRINT",FACE,{"disambiguationData":[TD([[makeQuery(id+"F0.imprint","IMPRINT",EDGE,{"derivedFrom":sQuery(id+"F0.wireOp",EDGE,"E256")}),-1.0]])]});
            var Q28;
            Q28=makeQuery(id+"F0.imprint","IMPRINT",FACE,{"disambiguationData":[TD([[makeQuery(id+"F0.imprint","IMPRINT",EDGE,{"derivedFrom":sQuery(id+"F0.wireOp",EDGE,"E276")}),-1.0]])]});
            var Q29;
            Q29=makeQuery(id+"F0.imprint","IMPRINT",FACE,{"disambiguationData":[TD([[makeQuery(id+"F0.imprint","IMPRINT",EDGE,{"derivedFrom":sQuery(id+"F0.wireOp",EDGE,"E68")}),-1.0]])]});
            var Q30;
            Q30=makeQuery(id+"F0.imprint","IMPRINT",FACE,{"disambiguationData":[TD([[makeQuery(id+"F0.imprint","IMPRINT",EDGE,{"derivedFrom":sQuery(id+"F0.wireOp",EDGE,"E36")}),-1.0]])]});
            var Q31;
            Q31=makeQuery(id+"F0.imprint","IMPRINT",FACE,{"disambiguationData":[TD([[makeQuery(id+"F0.imprint","IMPRINT",EDGE,{"derivedFrom":sQuery(id+"F0.wireOp",EDGE,"E192")}),-1.0]])]});
            var Q32;
            Q32=makeQuery(id+"F0.imprint","IMPRINT",FACE,{"disambiguationData":[TD([[makeQuery(id+"F0.imprint","IMPRINT",EDGE,{"derivedFrom":sQuery(id+"F0.wireOp",EDGE,"E80")}),-1.0]])]});
            var Q33;
            Q33=makeQuery(id+"F0.imprint","IMPRINT",FACE,{"disambiguationData":[TD([[makeQuery(id+"F0.imprint","IMPRINT",EDGE,{"derivedFrom":sQuery(id+"F0.wireOp",EDGE,"E48")}),-1.0]])]});
            var Q34;
            Q34=makeQuery(id+"F0.imprint","IMPRINT",FACE,{"disambiguationData":[TD([[makeQuery(id+"F0.imprint","IMPRINT",EDGE,{"derivedFrom":sQuery(id+"F0.wireOp",EDGE,"E20")}),-1.0]])]});
            var Q35;
            Q35=makeQuery(id+"F0.imprint","IMPRINT",FACE,{"disambiguationData":[TD([[makeQuery(id+"F0.imprint","IMPRINT",EDGE,{"derivedFrom":sQuery(id+"F0.wireOp",EDGE,"E56")}),-1.0]])]});
            var Q36;
            Q36=makeQuery(id+"F0.imprint","IMPRINT",FACE,{"disambiguationData":[TD([[makeQuery(id+"F0.imprint","IMPRINT",EDGE,{"derivedFrom":sQuery(id+"F0.wireOp",EDGE,"E0")}),-1.0]])]});
            var Q37;
            Q37=makeQuery(id+"F0.imprint","IMPRINT",FACE,{"disambiguationData":[TD([[makeQuery(id+"F0.imprint","IMPRINT",EDGE,{"derivedFrom":sQuery(id+"F0.wireOp",EDGE,"E72")}),-1.0]])]});
            var Q38;
            Q38=makeQuery(id+"F0.imprint","IMPRINT",FACE,{"disambiguationData":[TD([[makeQuery(id+"F0.imprint","IMPRINT",EDGE,{"derivedFrom":sQuery(id+"F0.wireOp",EDGE,"E264")}),-1.0]])]});
            var Q39;
            Q39=makeQuery(id+"F0.imprint","IMPRINT",FACE,{"disambiguationData":[TD([[makeQuery(id+"F0.imprint","IMPRINT",EDGE,{"derivedFrom":sQuery(id+"F0.wireOp",EDGE,"E240")}),-1.0]])]});
            var Q40;
            Q40=makeQuery(id+"F0.imprint","IMPRINT",FACE,{"disambiguationData":[TD([[makeQuery(id+"F0.imprint","IMPRINT",EDGE,{"derivedFrom":sQuery(id+"F0.wireOp",EDGE,"E96")}),-1.0]])]});
            var Q41;
            Q41=makeQuery(id+"F0.imprint","IMPRINT",FACE,{"disambiguationData":[TD([[makeQuery(id+"F0.imprint","IMPRINT",EDGE,{"derivedFrom":sQuery(id+"F0.wireOp",EDGE,"E84")}),-1.0]])]});
            var Q42;
            Q42=makeQuery(id+"F0.imprint","IMPRINT",FACE,{"disambiguationData":[TD([[makeQuery(id+"F0.imprint","IMPRINT",EDGE,{"derivedFrom":sQuery(id+"F0.wireOp",EDGE,"E12")}),-1.0]])]});
            var Q43;
            Q43=makeQuery(id+"F0.imprint","IMPRINT",FACE,{"disambiguationData":[TD([[makeQuery(id+"F0.imprint","IMPRINT",EDGE,{"derivedFrom":sQuery(id+"F0.wireOp",EDGE,"E100")}),-1.0]])]});
            var Q44;
            Q44=makeQuery(id+"F0.imprint","IMPRINT",FACE,{"disambiguationData":[TD([[makeQuery(id+"F0.imprint","IMPRINT",EDGE,{"derivedFrom":sQuery(id+"F0.wireOp",EDGE,"E184")}),-1.0]])]});
            var Q45;
            Q45=makeQuery(id+"F0.imprint","IMPRINT",FACE,{"disambiguationData":[TD([[makeQuery(id+"F0.imprint","IMPRINT",EDGE,{"derivedFrom":sQuery(id+"F0.wireOp",EDGE,"E4")}),-1.0]])]});
            var Q46;
            Q46=makeQuery(id+"F0.imprint","IMPRINT",FACE,{"disambiguationData":[TD([[makeQuery(id+"F0.imprint","IMPRINT",EDGE,{"derivedFrom":sQuery(id+"F0.wireOp",EDGE,"E236")}),-1.0]])]});
            var Q47;
            Q47=makeQuery(id+"F0.imprint","IMPRINT",FACE,{"disambiguationData":[TD([[makeQuery(id+"F0.imprint","IMPRINT",EDGE,{"derivedFrom":sQuery(id+"F0.wireOp",EDGE,"E272")}),-1.0]])]});
            var Q48;
            Q48=makeQuery(id+"F0.imprint","IMPRINT",FACE,{"disambiguationData":[TD([[makeQuery(id+"F0.imprint","IMPRINT",EDGE,{"derivedFrom":sQuery(id+"F0.wireOp",EDGE,"E124")}),-1.0]])]});
            var Q49;
            Q49=makeQuery(id+"F0.imprint","IMPRINT",FACE,{"disambiguationData":[TD([[makeQuery(id+"F0.imprint","IMPRINT",EDGE,{"derivedFrom":sQuery(id+"F0.wireOp",EDGE,"E76")}),-1.0]])]});
            var Q50;
            Q50=makeQuery(id+"F0.imprint","IMPRINT",FACE,{"disambiguationData":[TD([[makeQuery(id+"F0.imprint","IMPRINT",EDGE,{"derivedFrom":sQuery(id+"F0.wireOp",EDGE,"E88")}),-1.0]])]});
            var Q51;
            Q51=makeQuery(id+"F0.imprint","IMPRINT",FACE,{"disambiguationData":[TD([[makeQuery(id+"F0.imprint","IMPRINT",EDGE,{"derivedFrom":sQuery(id+"F0.wireOp",EDGE,"E28")}),-1.0]])]});
            var Q52;
            Q52=makeQuery(id+"F0.imprint","IMPRINT",FACE,{"disambiguationData":[TD([[makeQuery(id+"F0.imprint","IMPRINT",EDGE,{"derivedFrom":sQuery(id+"F0.wireOp",EDGE,"E188")}),-1.0]])]});
            var Q53;
            Q53=makeQuery(id+"F0.imprint","IMPRINT",FACE,{"disambiguationData":[TD([[makeQuery(id+"F0.imprint","IMPRINT",EDGE,{"derivedFrom":sQuery(id+"F0.wireOp",EDGE,"E144")}),-1.0]])]});
            var Q54;
            Q54=makeQuery(id+"F0.imprint","IMPRINT",FACE,{"disambiguationData":[TD([[makeQuery(id+"F0.imprint","IMPRINT",EDGE,{"derivedFrom":sQuery(id+"F0.wireOp",EDGE,"E260")}),-1.0]])]});
            var Q55;
            Q55=makeQuery(id+"F0.imprint","IMPRINT",FACE,{"disambiguationData":[TD([[makeQuery(id+"F0.imprint","IMPRINT",EDGE,{"derivedFrom":sQuery(id+"F0.wireOp",EDGE,"E132")}),-1.0]])]});
            var Q56;
            Q56=makeQuery(id+"F0.imprint","IMPRINT",FACE,{"disambiguationData":[TD([[makeQuery(id+"F0.imprint","IMPRINT",EDGE,{"derivedFrom":sQuery(id+"F0.wireOp",EDGE,"E136")}),-1.0]])]});
            var Q57;
            Q57=makeQuery(id+"F0.imprint","IMPRINT",FACE,{"disambiguationData":[TD([[makeQuery(id+"F0.imprint","IMPRINT",EDGE,{"derivedFrom":sQuery(id+"F0.wireOp",EDGE,"E108")}),-1.0]])]});
            var Q58;
            Q58=makeQuery(id+"F0.imprint","IMPRINT",FACE,{"disambiguationData":[TD([[makeQuery(id+"F0.imprint","IMPRINT",EDGE,{"derivedFrom":sQuery(id+"F0.wireOp",EDGE,"E16")}),-1.0]])]});
            var Q59;
            Q59=makeQuery(id+"F0.imprint","IMPRINT",FACE,{"disambiguationData":[TD([[makeQuery(id+"F0.imprint","IMPRINT",EDGE,{"derivedFrom":sQuery(id+"F0.wireOp",EDGE,"E116")}),-1.0]])]});
            var Q60;
            Q60=makeQuery(id+"F0.imprint","IMPRINT",FACE,{"disambiguationData":[TD([[makeQuery(id+"F0.imprint","IMPRINT",EDGE,{"derivedFrom":sQuery(id+"F0.wireOp",EDGE,"E112")}),-1.0]])]});
            var Q61;
            Q61=makeQuery(id+"F0.imprint","IMPRINT",FACE,{"disambiguationData":[TD([[makeQuery(id+"F0.imprint","IMPRINT",EDGE,{"derivedFrom":sQuery(id+"F0.wireOp",EDGE,"E200")}),-1.0]])]});
            var Q62;
            Q62=makeQuery(id+"F0.imprint","IMPRINT",FACE,{"disambiguationData":[TD([[makeQuery(id+"F0.imprint","IMPRINT",EDGE,{"derivedFrom":sQuery(id+"F0.wireOp",EDGE,"E120")}),-1.0]])]});
            var Q63;
            Q63=makeQuery(id+"F0.imprint","IMPRINT",FACE,{"disambiguationData":[TD([[makeQuery(id+"F0.imprint","IMPRINT",EDGE,{"derivedFrom":sQuery(id+"F0.wireOp",EDGE,"E212")}),-1.0]])]});
            var Q64;
            Q64=makeQuery(id+"F0.imprint","IMPRINT",FACE,{"disambiguationData":[TD([[makeQuery(id+"F0.imprint","IMPRINT",EDGE,{"derivedFrom":sQuery(id+"F0.wireOp",EDGE,"E64")}),-1.0]])]});
            var Q65;
            Q65=makeQuery(id+"F0.imprint","IMPRINT",FACE,{"disambiguationData":[TD([[makeQuery(id+"F0.imprint","IMPRINT",EDGE,{"derivedFrom":sQuery(id+"F0.wireOp",EDGE,"E172")}),-1.0]])]});
            var Q66;
            Q66=makeQuery(id+"F0.imprint","IMPRINT",FACE,{"disambiguationData":[TD([[makeQuery(id+"F0.imprint","IMPRINT",EDGE,{"derivedFrom":sQuery(id+"F0.wireOp",EDGE,"E248")}),-1.0]])]});
            var Q67;
            Q67=makeQuery(id+"F0.imprint","IMPRINT",FACE,{"disambiguationData":[TD([[makeQuery(id+"F0.imprint","IMPRINT",EDGE,{"derivedFrom":sQuery(id+"F0.wireOp",EDGE,"E148")}),-1.0]])]});
            var Q68;
            Q68=makeQuery(id+"F0.imprint","IMPRINT",FACE,{"disambiguationData":[TD([[makeQuery(id+"F0.imprint","IMPRINT",EDGE,{"derivedFrom":sQuery(id+"F0.wireOp",EDGE,"E160")}),-1.0]])]});
            var Q69;
            Q69=makeQuery(id+"F0.imprint","IMPRINT",FACE,{"disambiguationData":[TD([[makeQuery(id+"F0.imprint","IMPRINT",EDGE,{"derivedFrom":sQuery(id+"F0.wireOp",EDGE,"E40")}),-1.0]])]});
            var Q70;
            Q70=makeQuery(id+"F0.imprint","IMPRINT",FACE,{"disambiguationData":[TD([[makeQuery(id+"F0.imprint","IMPRINT",EDGE,{"derivedFrom":sQuery(id+"F0.wireOp",EDGE,"E52")}),-1.0]])]});
            var Q71;
            Q71=makeQuery(id+"F0.imprint","IMPRINT",FACE,{"disambiguationData":[TD([[makeQuery(id+"F0.imprint","IMPRINT",EDGE,{"derivedFrom":sQuery(id+"F0.wireOp",EDGE,"E224")}),-1.0]])]});
            extrude(context, id + "F1", {"entities" : qUnion([Q0, Q1, Q2, Q3, Q4, Q5, Q6, Q7, Q8, Q9, Q10, Q11, Q12, Q13, Q14, Q15, Q16, Q17, Q18, Q19, Q20, Q21, Q22, Q23, Q24, Q25, Q26, Q27, Q28, Q29, Q30, Q31, Q32, Q33, Q34, Q35, Q36, Q37, Q38, Q39, Q40, Q41, Q42, Q43, Q44, Q45, Q46, Q47, Q48, Q49, Q50, Q51, Q52, Q53, Q54, Q55, Q56, Q57, Q58, Q59, Q60, Q61, Q62, Q63, Q64, Q65, Q66, Q67, Q68, Q69, Q70, Q71]), "depth" : 3.2 * mm, "offsetDistance" : 25 * mm});
        }
        {
            var Q0;
            Q0=makeQuery(id+"F1.opExtrude","CAP_FACE",FACE,{"disambiguationData":[OSD([sQuery(id+"F0.wireOp",EDGE,"E184"),sQuery(id+"F0.wireOp",EDGE,"E185"),sQuery(id+"F0.wireOp",EDGE,"E186"),sQuery(id+"F0.wireOp",EDGE,"E187")])],"isStart":false});
            var sketch = newSketch(context, id + "F2", { "sketchPlane" : qUnion([Q0])});
            skLineSegment(sketch, "E288.bottom", {"start": v(-80.07, 65.1) * mm, "end": v(70.08, 65.1) * mm});
            skLineSegment(sketch, "E288.top", {"start": v(-80.07, 55.06) * mm, "end": v(70.08, 55.06) * mm});
            skLineSegment(sketch, "E288.left", {"start": v(-80.07, 65.1) * mm, "end": v(-80.07, 55.06) * mm});
            skLineSegment(sketch, "E288.right", {"start": v(70.08, 65.1) * mm, "end": v(70.08, 55.06) * mm});
            skLineSegment(sketch, "E289.bottom", {"start": v(70.08, 65.1) * mm, "end": v(79.86, 65.1) * mm});
            skLineSegment(sketch, "E289.top", {"start": v(70.08, -64.94) * mm, "end": v(79.86, -64.94) * mm});
            skLineSegment(sketch, "E289.left", {"start": v(70.08, 65.1) * mm, "end": v(70.08, -64.94) * mm});
            skLineSegment(sketch, "E289.right", {"start": v(79.86, 65.1) * mm, "end": v(79.86, -64.94) * mm});
            skLineSegment(sketch, "E290.bottom", {"start": v(70.08, -64.94) * mm, "end": v(-79.97, -64.94) * mm});
            skLineSegment(sketch, "E290.top", {"start": v(70.08, -54.93) * mm, "end": v(-79.97, -54.93) * mm});
            skLineSegment(sketch, "E290.left", {"start": v(70.08, -64.94) * mm, "end": v(70.08, -54.93) * mm});
            skLineSegment(sketch, "E290.right", {"start": v(-79.97, -64.94) * mm, "end": v(-79.97, -54.93) * mm});
            skSolve(sketch);
        }
        {
            var Q0;
            Q0=makeQuery(id+"F2.imprint","IMPRINT",FACE,{"disambiguationData":[TD([[makeQuery(id+"F2.imprint","IMPRINT",EDGE,{"derivedFrom":sQuery(id+"F2.wireOp",EDGE,"E290.bottom")}),-1.0]])]});
            var Q1;
            {var subQ3=sQuery(id+"F2.wireOp",EDGE,"E289.bottom");Q1=makeQuery(id+"F2.imprint","IMPRINT",FACE,{"disambiguationData":[TD([[makeQuery(id+"F2.imprint","IMPRINT",EDGE,{"derivedFrom":subQ3}),-1.0]])]});}
            var Q2;
            {var subQ1=sQuery(id+"F2.wireOp",EDGE,"E288.top");Q2=makeQuery(id+"F2.imprint","IMPRINT",FACE,{"disambiguationData":[TD([[makeQuery(id+"F2.imprint","IMPRINT",EDGE,{"derivedFrom":subQ1}),1.0]])]});}
            var Q3;
            {var subQ0=sQuery(id+"F2.wireOp",EDGE,"E288.left");var subQ1=sQuery(id+"F2.wireOp",EDGE,"E288.bottom");var subQ2=makeQuery(id+"F2.imprint","INTERSECT",VERTEX,{"derivedFrom":[subQ1,subQ0]});Q3=makeQuery(id+"F2.imprint","IMPRINT",FACE,{"disambiguationData":[TD([[makeQuery(id+"F2.imprint","IMPRINT",EDGE,{"disambiguationData":[TD([[subQ2,-1.0]])],"derivedFrom":subQ1}),-1.0]])]});}
            extrude(context, id + "F3", {"entities" : qUnion([Q0, Q1, Q2, Q3]), "depth" : .8 * mm, "offsetDistance" : 25 * mm, "hasSecondDirection" : true, "secondDirectionOppositeDirection" : true, "secondDirectionDepth" : 4 * mm});
        }
        {
            var Q0;
            Q0=makeQuery(id+"F3.opExtrude","CAP_FACE",FACE,{"disambiguationData":[OSD([sQuery(id+"F2.wireOp",EDGE,"E288.bottom"),sQuery(id+"F2.wireOp",EDGE,"E288.top"),sQuery(id+"F2.wireOp",EDGE,"E288.left"),sQuery(id+"F2.wireOp",EDGE,"E289.bottom"),sQuery(id+"F2.wireOp",EDGE,"E289.top"),sQuery(id+"F2.wireOp",EDGE,"E289.left"),sQuery(id+"F2.wireOp",EDGE,"E289.right"),sQuery(id+"F2.wireOp",EDGE,"E290.bottom"),sQuery(id+"F2.wireOp",EDGE,"E290.top"),sQuery(id+"F2.wireOp",EDGE,"E290.right")])],"isStart":false});
            var sketch = newSketch(context, id + "F4", { "sketchPlane" : qUnion([Q0])});
            skLineSegment(sketch, "E291", {"start": v(-80.6, -54.4) * mm, "end": v(-75.4, -54.4) * mm});
            skLineSegment(sketch, "E292", {"start": v(-75.4, -54.4) * mm, "end": v(-75.4, -65.6) * mm});
            skLineSegment(sketch, "E293", {"start": v(-75.4, -65.6) * mm, "end": v(-80.6, -65.6) * mm});
            skLineSegment(sketch, "E294", {"start": v(-80.6, -65.6) * mm, "end": v(-80.6, -54.4) * mm});
            skLineSegment(sketch, "E295", {"start": v(-71.6, -54.4) * mm, "end": v(-60.4, -54.4) * mm});
            skLineSegment(sketch, "E296", {"start": v(-60.4, -54.4) * mm, "end": v(-60.4, -59.6) * mm});
            skLineSegment(sketch, "E297", {"start": v(-60.4, -59.6) * mm, "end": v(-71.6, -59.6) * mm});
            skLineSegment(sketch, "E298", {"start": v(-71.6, -59.6) * mm, "end": v(-71.6, -54.4) * mm});
            skLineSegment(sketch, "E299", {"start": v(-71.6, -60.4) * mm, "end": v(-60.4, -60.4) * mm});
            skLineSegment(sketch, "E300", {"start": v(-60.4, -60.4) * mm, "end": v(-60.4, -65.6) * mm});
            skLineSegment(sketch, "E301", {"start": v(-60.4, -65.6) * mm, "end": v(-71.6, -65.6) * mm});
            skLineSegment(sketch, "E302", {"start": v(-71.6, -65.6) * mm, "end": v(-71.6, -60.4) * mm});
            skLineSegment(sketch, "E303", {"start": v(-59.6, -54.4) * mm, "end": v(-54.4, -54.4) * mm});
            skLineSegment(sketch, "E304", {"start": v(-54.4, -54.4) * mm, "end": v(-54.4, -65.6) * mm});
            skLineSegment(sketch, "E305", {"start": v(-54.4, -65.6) * mm, "end": v(-59.6, -65.6) * mm});
            skLineSegment(sketch, "E306", {"start": v(-59.6, -65.6) * mm, "end": v(-59.6, -54.4) * mm});
            skLineSegment(sketch, "E307", {"start": v(-53.6, -54.4) * mm, "end": v(-42.4, -54.4) * mm});
            skLineSegment(sketch, "E308", {"start": v(-42.4, -54.4) * mm, "end": v(-42.4, -59.6) * mm});
            skLineSegment(sketch, "E309", {"start": v(-42.4, -59.6) * mm, "end": v(-53.6, -59.6) * mm});
            skLineSegment(sketch, "E310", {"start": v(-53.6, -59.6) * mm, "end": v(-53.6, -54.4) * mm});
            skLineSegment(sketch, "E311", {"start": v(-53.6, -60.4) * mm, "end": v(-42.4, -60.4) * mm});
            skLineSegment(sketch, "E312", {"start": v(-42.4, -60.4) * mm, "end": v(-42.4, -65.6) * mm});
            skLineSegment(sketch, "E313", {"start": v(-42.4, -65.6) * mm, "end": v(-53.6, -65.6) * mm});
            skLineSegment(sketch, "E314", {"start": v(-53.6, -65.6) * mm, "end": v(-53.6, -60.4) * mm});
            skLineSegment(sketch, "E315", {"start": v(-41.6, -54.4) * mm, "end": v(-36.4, -54.4) * mm});
            skLineSegment(sketch, "E316", {"start": v(-36.4, -54.4) * mm, "end": v(-36.4, -65.6) * mm});
            skLineSegment(sketch, "E317", {"start": v(-36.4, -65.6) * mm, "end": v(-41.6, -65.6) * mm});
            skLineSegment(sketch, "E318", {"start": v(-41.6, -65.6) * mm, "end": v(-41.6, -54.4) * mm});
            skLineSegment(sketch, "E319", {"start": v(-35.6, -54.4) * mm, "end": v(-24.4, -54.4) * mm});
            skLineSegment(sketch, "E320", {"start": v(-24.4, -54.4) * mm, "end": v(-24.4, -59.6) * mm});
            skLineSegment(sketch, "E321", {"start": v(-24.4, -59.6) * mm, "end": v(-35.6, -59.6) * mm});
            skLineSegment(sketch, "E322", {"start": v(-35.6, -59.6) * mm, "end": v(-35.6, -54.4) * mm});
            skLineSegment(sketch, "E323", {"start": v(-35.6, -60.4) * mm, "end": v(-24.4, -60.4) * mm});
            skLineSegment(sketch, "E324", {"start": v(-24.4, -60.4) * mm, "end": v(-24.4, -65.6) * mm});
            skLineSegment(sketch, "E325", {"start": v(-24.4, -65.6) * mm, "end": v(-35.6, -65.6) * mm});
            skLineSegment(sketch, "E326", {"start": v(-35.6, -65.6) * mm, "end": v(-35.6, -60.4) * mm});
            skLineSegment(sketch, "E327", {"start": v(-23.6, -54.4) * mm, "end": v(-18.4, -54.4) * mm});
            skLineSegment(sketch, "E328", {"start": v(-18.4, -54.4) * mm, "end": v(-18.4, -65.6) * mm});
            skLineSegment(sketch, "E329", {"start": v(-18.4, -65.6) * mm, "end": v(-23.6, -65.6) * mm});
            skLineSegment(sketch, "E330", {"start": v(-23.6, -65.6) * mm, "end": v(-23.6, -54.4) * mm});
            skLineSegment(sketch, "E331", {"start": v(-17.6, -54.4) * mm, "end": v(-6.4, -54.4) * mm});
            skLineSegment(sketch, "E332", {"start": v(-6.4, -54.4) * mm, "end": v(-6.4, -59.6) * mm});
            skLineSegment(sketch, "E333", {"start": v(-6.4, -59.6) * mm, "end": v(-17.6, -59.6) * mm});
            skLineSegment(sketch, "E334", {"start": v(-17.6, -59.6) * mm, "end": v(-17.6, -54.4) * mm});
            skLineSegment(sketch, "E335", {"start": v(-17.6, -60.4) * mm, "end": v(-6.4, -60.4) * mm});
            skLineSegment(sketch, "E336", {"start": v(-6.4, -60.4) * mm, "end": v(-6.4, -65.6) * mm});
            skLineSegment(sketch, "E337", {"start": v(-6.4, -65.6) * mm, "end": v(-17.6, -65.6) * mm});
            skLineSegment(sketch, "E338", {"start": v(-17.6, -65.6) * mm, "end": v(-17.6, -60.4) * mm});
            skLineSegment(sketch, "E339", {"start": v(-5.6, -54.4) * mm, "end": v(-0.4, -54.4) * mm});
            skLineSegment(sketch, "E340", {"start": v(-0.4, -54.4) * mm, "end": v(-0.4, -65.6) * mm});
            skLineSegment(sketch, "E341", {"start": v(-0.4, -65.6) * mm, "end": v(-5.6, -65.6) * mm});
            skLineSegment(sketch, "E342", {"start": v(-5.6, -65.6) * mm, "end": v(-5.6, -54.4) * mm});
            skLineSegment(sketch, "E343", {"start": v(0.4, -54.4) * mm, "end": v(11.6, -54.4) * mm});
            skLineSegment(sketch, "E344", {"start": v(11.6, -54.4) * mm, "end": v(11.6, -59.6) * mm});
            skLineSegment(sketch, "E345", {"start": v(11.6, -59.6) * mm, "end": v(0.4, -59.6) * mm});
            skLineSegment(sketch, "E346", {"start": v(0.4, -59.6) * mm, "end": v(0.4, -54.4) * mm});
            skLineSegment(sketch, "E347", {"start": v(0.4, -60.4) * mm, "end": v(11.6, -60.4) * mm});
            skLineSegment(sketch, "E348", {"start": v(11.6, -60.4) * mm, "end": v(11.6, -65.6) * mm});
            skLineSegment(sketch, "E349", {"start": v(11.6, -65.6) * mm, "end": v(0.4, -65.6) * mm});
            skLineSegment(sketch, "E350", {"start": v(0.4, -65.6) * mm, "end": v(0.4, -60.4) * mm});
            skLineSegment(sketch, "E351", {"start": v(12.4, -54.4) * mm, "end": v(17.6, -54.4) * mm});
            skLineSegment(sketch, "E352", {"start": v(17.6, -54.4) * mm, "end": v(17.6, -65.6) * mm});
            skLineSegment(sketch, "E353", {"start": v(17.6, -65.6) * mm, "end": v(12.4, -65.6) * mm});
            skLineSegment(sketch, "E354", {"start": v(12.4, -65.6) * mm, "end": v(12.4, -54.4) * mm});
            skLineSegment(sketch, "E355", {"start": v(18.4, -54.4) * mm, "end": v(29.6, -54.4) * mm});
            skLineSegment(sketch, "E356", {"start": v(29.6, -54.4) * mm, "end": v(29.6, -59.6) * mm});
            skLineSegment(sketch, "E357", {"start": v(29.6, -59.6) * mm, "end": v(18.4, -59.6) * mm});
            skLineSegment(sketch, "E358", {"start": v(18.4, -59.6) * mm, "end": v(18.4, -54.4) * mm});
            skLineSegment(sketch, "E359", {"start": v(18.4, -60.4) * mm, "end": v(29.6, -60.4) * mm});
            skLineSegment(sketch, "E360", {"start": v(29.6, -60.4) * mm, "end": v(29.6, -65.6) * mm});
            skLineSegment(sketch, "E361", {"start": v(29.6, -65.6) * mm, "end": v(18.4, -65.6) * mm});
            skLineSegment(sketch, "E362", {"start": v(18.4, -65.6) * mm, "end": v(18.4, -60.4) * mm});
            skLineSegment(sketch, "E363", {"start": v(30.4, -54.4) * mm, "end": v(35.6, -54.4) * mm});
            skLineSegment(sketch, "E364", {"start": v(35.6, -54.4) * mm, "end": v(35.6, -65.6) * mm});
            skLineSegment(sketch, "E365", {"start": v(35.6, -65.6) * mm, "end": v(30.4, -65.6) * mm});
            skLineSegment(sketch, "E366", {"start": v(30.4, -65.6) * mm, "end": v(30.4, -54.4) * mm});
            skLineSegment(sketch, "E367", {"start": v(36.4, -54.4) * mm, "end": v(47.6, -54.4) * mm});
            skLineSegment(sketch, "E368", {"start": v(47.6, -54.4) * mm, "end": v(47.6, -59.6) * mm});
            skLineSegment(sketch, "E369", {"start": v(47.6, -59.6) * mm, "end": v(36.4, -59.6) * mm});
            skLineSegment(sketch, "E370", {"start": v(36.4, -59.6) * mm, "end": v(36.4, -54.4) * mm});
            skLineSegment(sketch, "E371", {"start": v(36.4, -60.4) * mm, "end": v(47.6, -60.4) * mm});
            skLineSegment(sketch, "E372", {"start": v(47.6, -60.4) * mm, "end": v(47.6, -65.6) * mm});
            skLineSegment(sketch, "E373", {"start": v(47.6, -65.6) * mm, "end": v(36.4, -65.6) * mm});
            skLineSegment(sketch, "E374", {"start": v(36.4, -65.6) * mm, "end": v(36.4, -60.4) * mm});
            skLineSegment(sketch, "E375", {"start": v(48.4, -54.4) * mm, "end": v(53.6, -54.4) * mm});
            skLineSegment(sketch, "E376", {"start": v(53.6, -54.4) * mm, "end": v(53.6, -65.6) * mm});
            skLineSegment(sketch, "E377", {"start": v(53.6, -65.6) * mm, "end": v(48.4, -65.6) * mm});
            skLineSegment(sketch, "E378", {"start": v(48.4, -65.6) * mm, "end": v(48.4, -54.4) * mm});
            skLineSegment(sketch, "E379", {"start": v(54.4, -54.4) * mm, "end": v(65.6, -54.4) * mm});
            skLineSegment(sketch, "E380", {"start": v(65.6, -54.4) * mm, "end": v(65.6, -59.6) * mm});
            skLineSegment(sketch, "E381", {"start": v(65.6, -59.6) * mm, "end": v(54.4, -59.6) * mm});
            skLineSegment(sketch, "E382", {"start": v(54.4, -59.6) * mm, "end": v(54.4, -54.4) * mm});
            skLineSegment(sketch, "E383", {"start": v(54.4, -60.4) * mm, "end": v(65.6, -60.4) * mm});
            skLineSegment(sketch, "E384", {"start": v(65.6, -60.4) * mm, "end": v(65.6, -65.6) * mm});
            skLineSegment(sketch, "E385", {"start": v(65.6, -65.6) * mm, "end": v(54.4, -65.6) * mm});
            skLineSegment(sketch, "E386", {"start": v(54.4, -65.6) * mm, "end": v(54.4, -60.4) * mm});
            skLineSegment(sketch, "E387", {"start": v(66.4, -60.4) * mm, "end": v(71.6, -60.4) * mm});
            skLineSegment(sketch, "E388", {"start": v(71.6, -60.4) * mm, "end": v(71.6, -65.6) * mm});
            skLineSegment(sketch, "E389", {"start": v(71.6, -65.6) * mm, "end": v(66.4, -65.6) * mm});
            skLineSegment(sketch, "E390", {"start": v(66.4, -65.6) * mm, "end": v(66.4, -60.4) * mm});
            skLineSegment(sketch, "E391", {"start": v(66.43, -54.4) * mm, "end": v(68.63, -54.4) * mm});
            skLineSegment(sketch, "E392", {"start": v(68.63, -54.4) * mm, "end": v(68.63, -59.6) * mm});
            skLineSegment(sketch, "E393", {"start": v(68.63, -59.6) * mm, "end": v(66.43, -59.6) * mm});
            skLineSegment(sketch, "E394", {"start": v(66.43, -59.6) * mm, "end": v(66.43, -54.4) * mm});
            skLineSegment(sketch, "E395", {"start": v(72.4, -60.4) * mm, "end": v(80.6, -60.4) * mm});
            skLineSegment(sketch, "E396", {"start": v(80.6, -60.4) * mm, "end": v(80.6, -65.6) * mm});
            skLineSegment(sketch, "E397", {"start": v(80.6, -65.6) * mm, "end": v(72.4, -65.6) * mm});
            skLineSegment(sketch, "E398", {"start": v(72.4, -65.6) * mm, "end": v(72.4, -60.4) * mm});
            skLineSegment(sketch, "E399", {"start": v(-74.6, -54.4) * mm, "end": v(-72.4, -54.4) * mm});
            skLineSegment(sketch, "E400", {"start": v(-72.4, -54.4) * mm, "end": v(-72.4, -59.6) * mm});
            skLineSegment(sketch, "E401", {"start": v(-72.4, -59.6) * mm, "end": v(-74.6, -59.6) * mm});
            skLineSegment(sketch, "E402", {"start": v(-74.6, -59.6) * mm, "end": v(-74.6, -54.4) * mm});
            skLineSegment(sketch, "E403", {"start": v(-74.6, -60.4) * mm, "end": v(-72.4, -60.4) * mm});
            skLineSegment(sketch, "E404", {"start": v(-72.4, -60.4) * mm, "end": v(-72.4, -65.6) * mm});
            skLineSegment(sketch, "E405", {"start": v(-72.4, -65.6) * mm, "end": v(-74.6, -65.6) * mm});
            skLineSegment(sketch, "E406", {"start": v(-74.6, -65.6) * mm, "end": v(-74.6, -60.4) * mm});
            skLineSegment(sketch, "E407", {"start": v(75.4, -48.42) * mm, "end": v(80.6, -48.42) * mm});
            skLineSegment(sketch, "E408", {"start": v(80.6, -48.42) * mm, "end": v(80.6, -59.6) * mm});
            skLineSegment(sketch, "E409", {"start": v(80.6, -59.6) * mm, "end": v(75.4, -59.6) * mm});
            skLineSegment(sketch, "E410", {"start": v(75.4, -59.6) * mm, "end": v(75.4, -48.42) * mm});
            skLineSegment(sketch, "E411", {"start": v(69.39, -44.6) * mm, "end": v(69.39, -33.4) * mm});
            skLineSegment(sketch, "E412", {"start": v(69.39, -33.4) * mm, "end": v(74.59, -33.4) * mm});
            skLineSegment(sketch, "E413", {"start": v(74.59, -33.4) * mm, "end": v(74.59, -44.6) * mm});
            skLineSegment(sketch, "E414", {"start": v(74.59, -44.6) * mm, "end": v(69.39, -44.6) * mm});
            skLineSegment(sketch, "E415", {"start": v(69.39, -32.6) * mm, "end": v(69.39, -27.4) * mm});
            skLineSegment(sketch, "E416", {"start": v(69.39, -27.4) * mm, "end": v(80.59, -27.4) * mm});
            skLineSegment(sketch, "E417", {"start": v(80.59, -27.4) * mm, "end": v(80.59, -32.6) * mm});
            skLineSegment(sketch, "E418", {"start": v(80.59, -32.6) * mm, "end": v(69.39, -32.6) * mm});
            skLineSegment(sketch, "E419", {"start": v(75.39, -44.6) * mm, "end": v(75.39, -33.4) * mm});
            skLineSegment(sketch, "E420", {"start": v(75.39, -33.4) * mm, "end": v(80.59, -33.4) * mm});
            skLineSegment(sketch, "E421", {"start": v(80.59, -33.4) * mm, "end": v(80.59, -44.6) * mm});
            skLineSegment(sketch, "E422", {"start": v(80.59, -44.6) * mm, "end": v(75.39, -44.6) * mm});
            skLineSegment(sketch, "E423", {"start": v(69.39, -26.6) * mm, "end": v(69.39, -15.4) * mm});
            skLineSegment(sketch, "E424", {"start": v(69.39, -15.4) * mm, "end": v(74.59, -15.4) * mm});
            skLineSegment(sketch, "E425", {"start": v(74.59, -15.4) * mm, "end": v(74.59, -26.6) * mm});
            skLineSegment(sketch, "E426", {"start": v(74.59, -26.6) * mm, "end": v(69.39, -26.6) * mm});
            skLineSegment(sketch, "E427", {"start": v(69.39, -14.6) * mm, "end": v(69.39, -9.4) * mm});
            skLineSegment(sketch, "E428", {"start": v(69.39, -9.4) * mm, "end": v(80.59, -9.4) * mm});
            skLineSegment(sketch, "E429", {"start": v(80.59, -9.4) * mm, "end": v(80.59, -14.6) * mm});
            skLineSegment(sketch, "E430", {"start": v(80.59, -14.6) * mm, "end": v(69.39, -14.6) * mm});
            skLineSegment(sketch, "E431", {"start": v(75.39, -26.6) * mm, "end": v(75.39, -15.4) * mm});
            skLineSegment(sketch, "E432", {"start": v(75.39, -15.4) * mm, "end": v(80.59, -15.4) * mm});
            skLineSegment(sketch, "E433", {"start": v(80.59, -15.4) * mm, "end": v(80.59, -26.6) * mm});
            skLineSegment(sketch, "E434", {"start": v(80.59, -26.6) * mm, "end": v(75.39, -26.6) * mm});
            skLineSegment(sketch, "E435", {"start": v(69.39, -8.6) * mm, "end": v(69.39, 2.6) * mm});
            skLineSegment(sketch, "E436", {"start": v(69.39, 2.6) * mm, "end": v(74.59, 2.6) * mm});
            skLineSegment(sketch, "E437", {"start": v(74.59, 2.6) * mm, "end": v(74.59, -8.6) * mm});
            skLineSegment(sketch, "E438", {"start": v(74.59, -8.6) * mm, "end": v(69.39, -8.6) * mm});
            skLineSegment(sketch, "E439", {"start": v(69.39, 3.4) * mm, "end": v(69.39, 8.6) * mm});
            skLineSegment(sketch, "E440", {"start": v(69.39, 8.6) * mm, "end": v(80.59, 8.6) * mm});
            skLineSegment(sketch, "E441", {"start": v(80.59, 8.6) * mm, "end": v(80.59, 3.4) * mm});
            skLineSegment(sketch, "E442", {"start": v(80.59, 3.4) * mm, "end": v(69.39, 3.4) * mm});
            skLineSegment(sketch, "E443", {"start": v(75.39, -8.6) * mm, "end": v(75.39, 2.6) * mm});
            skLineSegment(sketch, "E444", {"start": v(75.39, 2.6) * mm, "end": v(80.59, 2.6) * mm});
            skLineSegment(sketch, "E445", {"start": v(80.59, 2.6) * mm, "end": v(80.59, -8.6) * mm});
            skLineSegment(sketch, "E446", {"start": v(80.59, -8.6) * mm, "end": v(75.39, -8.6) * mm});
            skLineSegment(sketch, "E447", {"start": v(69.39, 9.4) * mm, "end": v(69.39, 20.6) * mm});
            skLineSegment(sketch, "E448", {"start": v(69.39, 20.6) * mm, "end": v(74.59, 20.6) * mm});
            skLineSegment(sketch, "E449", {"start": v(74.59, 20.6) * mm, "end": v(74.59, 9.4) * mm});
            skLineSegment(sketch, "E450", {"start": v(74.59, 9.4) * mm, "end": v(69.39, 9.4) * mm});
            skLineSegment(sketch, "E451", {"start": v(69.39, 21.4) * mm, "end": v(69.39, 26.6) * mm});
            skLineSegment(sketch, "E452", {"start": v(69.39, 26.6) * mm, "end": v(80.59, 26.6) * mm});
            skLineSegment(sketch, "E453", {"start": v(80.59, 26.6) * mm, "end": v(80.59, 21.4) * mm});
            skLineSegment(sketch, "E454", {"start": v(80.59, 21.4) * mm, "end": v(69.39, 21.4) * mm});
            skLineSegment(sketch, "E455", {"start": v(75.39, 9.4) * mm, "end": v(75.39, 20.6) * mm});
            skLineSegment(sketch, "E456", {"start": v(75.39, 20.6) * mm, "end": v(80.59, 20.6) * mm});
            skLineSegment(sketch, "E457", {"start": v(80.59, 20.6) * mm, "end": v(80.59, 9.4) * mm});
            skLineSegment(sketch, "E458", {"start": v(80.59, 9.4) * mm, "end": v(75.39, 9.4) * mm});
            skLineSegment(sketch, "E459", {"start": v(69.39, 27.4) * mm, "end": v(69.39, 38.6) * mm});
            skLineSegment(sketch, "E460", {"start": v(69.39, 38.6) * mm, "end": v(74.59, 38.6) * mm});
            skLineSegment(sketch, "E461", {"start": v(74.59, 38.6) * mm, "end": v(74.59, 27.4) * mm});
            skLineSegment(sketch, "E462", {"start": v(74.59, 27.4) * mm, "end": v(69.39, 27.4) * mm});
            skLineSegment(sketch, "E463", {"start": v(69.39, 39.4) * mm, "end": v(69.39, 44.6) * mm});
            skLineSegment(sketch, "E464", {"start": v(69.39, 44.6) * mm, "end": v(80.59, 44.6) * mm});
            skLineSegment(sketch, "E465", {"start": v(80.59, 44.6) * mm, "end": v(80.59, 39.4) * mm});
            skLineSegment(sketch, "E466", {"start": v(80.59, 39.4) * mm, "end": v(69.39, 39.4) * mm});
            skLineSegment(sketch, "E467", {"start": v(75.39, 27.4) * mm, "end": v(75.39, 38.6) * mm});
            skLineSegment(sketch, "E468", {"start": v(75.39, 38.6) * mm, "end": v(80.59, 38.6) * mm});
            skLineSegment(sketch, "E469", {"start": v(80.59, 38.6) * mm, "end": v(80.59, 27.4) * mm});
            skLineSegment(sketch, "E470", {"start": v(80.59, 27.4) * mm, "end": v(75.39, 27.4) * mm});
            skLineSegment(sketch, "E471", {"start": v(69.39, 45.4) * mm, "end": v(69.39, 56.6) * mm});
            skLineSegment(sketch, "E472", {"start": v(69.39, 56.6) * mm, "end": v(74.59, 56.6) * mm});
            skLineSegment(sketch, "E473", {"start": v(74.59, 56.6) * mm, "end": v(74.59, 45.4) * mm});
            skLineSegment(sketch, "E474", {"start": v(74.59, 45.4) * mm, "end": v(69.39, 45.4) * mm});
            skLineSegment(sketch, "E475", {"start": v(69.37, 60.36) * mm, "end": v(69.37, 65.56) * mm});
            skLineSegment(sketch, "E476", {"start": v(69.37, 65.56) * mm, "end": v(80.57, 65.56) * mm});
            skLineSegment(sketch, "E477", {"start": v(80.57, 65.56) * mm, "end": v(80.57, 60.36) * mm});
            skLineSegment(sketch, "E478", {"start": v(80.57, 60.36) * mm, "end": v(69.37, 60.36) * mm});
            skLineSegment(sketch, "E479", {"start": v(75.39, 45.4) * mm, "end": v(75.39, 56.6) * mm});
            skLineSegment(sketch, "E480", {"start": v(75.39, 56.6) * mm, "end": v(80.59, 56.6) * mm});
            skLineSegment(sketch, "E481", {"start": v(80.59, 56.6) * mm, "end": v(80.59, 45.4) * mm});
            skLineSegment(sketch, "E482", {"start": v(80.59, 45.4) * mm, "end": v(75.39, 45.4) * mm});
            skLineSegment(sketch, "E483", {"start": v(-80.6, 65.6) * mm, "end": v(-75.4, 65.6) * mm});
            skLineSegment(sketch, "E484", {"start": v(-75.4, 65.6) * mm, "end": v(-75.4, 54.4) * mm});
            skLineSegment(sketch, "E485", {"start": v(-75.4, 54.4) * mm, "end": v(-80.6, 54.4) * mm});
            skLineSegment(sketch, "E486", {"start": v(-80.6, 54.4) * mm, "end": v(-80.6, 65.6) * mm});
            skLineSegment(sketch, "E487", {"start": v(-71.6, 65.6) * mm, "end": v(-60.4, 65.6) * mm});
            skLineSegment(sketch, "E488", {"start": v(-60.4, 65.6) * mm, "end": v(-60.4, 60.4) * mm});
            skLineSegment(sketch, "E489", {"start": v(-60.4, 60.4) * mm, "end": v(-71.6, 60.4) * mm});
            skLineSegment(sketch, "E490", {"start": v(-71.6, 60.4) * mm, "end": v(-71.6, 65.6) * mm});
            skLineSegment(sketch, "E491", {"start": v(-71.6, 59.6) * mm, "end": v(-60.4, 59.6) * mm});
            skLineSegment(sketch, "E492", {"start": v(-60.4, 59.6) * mm, "end": v(-60.4, 54.4) * mm});
            skLineSegment(sketch, "E493", {"start": v(-60.4, 54.4) * mm, "end": v(-71.6, 54.4) * mm});
            skLineSegment(sketch, "E494", {"start": v(-71.6, 54.4) * mm, "end": v(-71.6, 59.6) * mm});
            skLineSegment(sketch, "E495", {"start": v(-59.6, 65.6) * mm, "end": v(-54.4, 65.6) * mm});
            skLineSegment(sketch, "E496", {"start": v(-54.4, 65.6) * mm, "end": v(-54.4, 54.4) * mm});
            skLineSegment(sketch, "E497", {"start": v(-54.4, 54.4) * mm, "end": v(-59.6, 54.4) * mm});
            skLineSegment(sketch, "E498", {"start": v(-59.6, 54.4) * mm, "end": v(-59.6, 65.6) * mm});
            skLineSegment(sketch, "E499", {"start": v(-53.6, 65.6) * mm, "end": v(-42.4, 65.6) * mm});
            skLineSegment(sketch, "E500", {"start": v(-42.4, 65.6) * mm, "end": v(-42.4, 60.4) * mm});
            skLineSegment(sketch, "E501", {"start": v(-42.4, 60.4) * mm, "end": v(-53.6, 60.4) * mm});
            skLineSegment(sketch, "E502", {"start": v(-53.6, 60.4) * mm, "end": v(-53.6, 65.6) * mm});
            skLineSegment(sketch, "E503", {"start": v(-53.6, 59.6) * mm, "end": v(-42.4, 59.6) * mm});
            skLineSegment(sketch, "E504", {"start": v(-42.4, 59.6) * mm, "end": v(-42.4, 54.4) * mm});
            skLineSegment(sketch, "E505", {"start": v(-42.4, 54.4) * mm, "end": v(-53.6, 54.4) * mm});
            skLineSegment(sketch, "E506", {"start": v(-53.6, 54.4) * mm, "end": v(-53.6, 59.6) * mm});
            skLineSegment(sketch, "E507", {"start": v(-41.6, 65.6) * mm, "end": v(-36.4, 65.6) * mm});
            skLineSegment(sketch, "E508", {"start": v(-36.4, 65.6) * mm, "end": v(-36.4, 54.4) * mm});
            skLineSegment(sketch, "E509", {"start": v(-36.4, 54.4) * mm, "end": v(-41.6, 54.4) * mm});
            skLineSegment(sketch, "E510", {"start": v(-41.6, 54.4) * mm, "end": v(-41.6, 65.6) * mm});
            skLineSegment(sketch, "E511", {"start": v(-35.6, 65.6) * mm, "end": v(-24.4, 65.6) * mm});
            skLineSegment(sketch, "E512", {"start": v(-24.4, 65.6) * mm, "end": v(-24.4, 60.4) * mm});
            skLineSegment(sketch, "E513", {"start": v(-24.4, 60.4) * mm, "end": v(-35.6, 60.4) * mm});
            skLineSegment(sketch, "E514", {"start": v(-35.6, 60.4) * mm, "end": v(-35.6, 65.6) * mm});
            skLineSegment(sketch, "E515", {"start": v(-35.6, 59.6) * mm, "end": v(-24.4, 59.6) * mm});
            skLineSegment(sketch, "E516", {"start": v(-24.4, 59.6) * mm, "end": v(-24.4, 54.4) * mm});
            skLineSegment(sketch, "E517", {"start": v(-24.4, 54.4) * mm, "end": v(-35.6, 54.4) * mm});
            skLineSegment(sketch, "E518", {"start": v(-35.6, 54.4) * mm, "end": v(-35.6, 59.6) * mm});
            skLineSegment(sketch, "E519", {"start": v(-23.6, 65.6) * mm, "end": v(-18.4, 65.6) * mm});
            skLineSegment(sketch, "E520", {"start": v(-18.4, 65.6) * mm, "end": v(-18.4, 54.4) * mm});
            skLineSegment(sketch, "E521", {"start": v(-18.4, 54.4) * mm, "end": v(-23.6, 54.4) * mm});
            skLineSegment(sketch, "E522", {"start": v(-23.6, 54.4) * mm, "end": v(-23.6, 65.6) * mm});
            skLineSegment(sketch, "E523", {"start": v(-17.6, 65.6) * mm, "end": v(-6.4, 65.6) * mm});
            skLineSegment(sketch, "E524", {"start": v(-6.4, 65.6) * mm, "end": v(-6.4, 60.4) * mm});
            skLineSegment(sketch, "E525", {"start": v(-6.4, 60.4) * mm, "end": v(-17.6, 60.4) * mm});
            skLineSegment(sketch, "E526", {"start": v(-17.6, 60.4) * mm, "end": v(-17.6, 65.6) * mm});
            skLineSegment(sketch, "E527", {"start": v(-17.6, 59.6) * mm, "end": v(-6.4, 59.6) * mm});
            skLineSegment(sketch, "E528", {"start": v(-6.4, 59.6) * mm, "end": v(-6.4, 54.4) * mm});
            skLineSegment(sketch, "E529", {"start": v(-6.4, 54.4) * mm, "end": v(-17.6, 54.4) * mm});
            skLineSegment(sketch, "E530", {"start": v(-17.6, 54.4) * mm, "end": v(-17.6, 59.6) * mm});
            skLineSegment(sketch, "E531", {"start": v(-5.6, 65.6) * mm, "end": v(-0.4, 65.6) * mm});
            skLineSegment(sketch, "E532", {"start": v(-0.4, 65.6) * mm, "end": v(-0.4, 54.4) * mm});
            skLineSegment(sketch, "E533", {"start": v(-0.4, 54.4) * mm, "end": v(-5.6, 54.4) * mm});
            skLineSegment(sketch, "E534", {"start": v(-5.6, 54.4) * mm, "end": v(-5.6, 65.6) * mm});
            skLineSegment(sketch, "E535", {"start": v(0.4, 65.6) * mm, "end": v(11.6, 65.6) * mm});
            skLineSegment(sketch, "E536", {"start": v(11.6, 65.6) * mm, "end": v(11.6, 60.4) * mm});
            skLineSegment(sketch, "E537", {"start": v(11.6, 60.4) * mm, "end": v(0.4, 60.4) * mm});
            skLineSegment(sketch, "E538", {"start": v(0.4, 60.4) * mm, "end": v(0.4, 65.6) * mm});
            skLineSegment(sketch, "E539", {"start": v(0.4, 59.6) * mm, "end": v(11.6, 59.6) * mm});
            skLineSegment(sketch, "E540", {"start": v(11.6, 59.6) * mm, "end": v(11.6, 54.4) * mm});
            skLineSegment(sketch, "E541", {"start": v(11.6, 54.4) * mm, "end": v(0.4, 54.4) * mm});
            skLineSegment(sketch, "E542", {"start": v(0.4, 54.4) * mm, "end": v(0.4, 59.6) * mm});
            skLineSegment(sketch, "E543", {"start": v(12.4, 65.6) * mm, "end": v(17.6, 65.6) * mm});
            skLineSegment(sketch, "E544", {"start": v(17.6, 65.6) * mm, "end": v(17.6, 54.4) * mm});
            skLineSegment(sketch, "E545", {"start": v(17.6, 54.4) * mm, "end": v(12.4, 54.4) * mm});
            skLineSegment(sketch, "E546", {"start": v(12.4, 54.4) * mm, "end": v(12.4, 65.6) * mm});
            skLineSegment(sketch, "E547", {"start": v(18.4, 65.6) * mm, "end": v(29.6, 65.6) * mm});
            skLineSegment(sketch, "E548", {"start": v(29.6, 65.6) * mm, "end": v(29.6, 60.4) * mm});
            skLineSegment(sketch, "E549", {"start": v(29.6, 60.4) * mm, "end": v(18.4, 60.4) * mm});
            skLineSegment(sketch, "E550", {"start": v(18.4, 60.4) * mm, "end": v(18.4, 65.6) * mm});
            skLineSegment(sketch, "E551", {"start": v(18.4, 59.6) * mm, "end": v(29.6, 59.6) * mm});
            skLineSegment(sketch, "E552", {"start": v(29.6, 59.6) * mm, "end": v(29.6, 54.4) * mm});
            skLineSegment(sketch, "E553", {"start": v(29.6, 54.4) * mm, "end": v(18.4, 54.4) * mm});
            skLineSegment(sketch, "E554", {"start": v(18.4, 54.4) * mm, "end": v(18.4, 59.6) * mm});
            skLineSegment(sketch, "E555", {"start": v(30.4, 65.6) * mm, "end": v(35.6, 65.6) * mm});
            skLineSegment(sketch, "E556", {"start": v(35.6, 65.6) * mm, "end": v(35.6, 54.4) * mm});
            skLineSegment(sketch, "E557", {"start": v(35.6, 54.4) * mm, "end": v(30.4, 54.4) * mm});
            skLineSegment(sketch, "E558", {"start": v(30.4, 54.4) * mm, "end": v(30.4, 65.6) * mm});
            skLineSegment(sketch, "E559", {"start": v(36.4, 65.6) * mm, "end": v(47.6, 65.6) * mm});
            skLineSegment(sketch, "E560", {"start": v(47.6, 65.6) * mm, "end": v(47.6, 60.4) * mm});
            skLineSegment(sketch, "E561", {"start": v(47.6, 60.4) * mm, "end": v(36.4, 60.4) * mm});
            skLineSegment(sketch, "E562", {"start": v(36.4, 60.4) * mm, "end": v(36.4, 65.6) * mm});
            skLineSegment(sketch, "E563", {"start": v(36.4, 59.6) * mm, "end": v(47.6, 59.6) * mm});
            skLineSegment(sketch, "E564", {"start": v(47.6, 59.6) * mm, "end": v(47.6, 54.4) * mm});
            skLineSegment(sketch, "E565", {"start": v(47.6, 54.4) * mm, "end": v(36.4, 54.4) * mm});
            skLineSegment(sketch, "E566", {"start": v(36.4, 54.4) * mm, "end": v(36.4, 59.6) * mm});
            skLineSegment(sketch, "E567", {"start": v(48.4, 65.6) * mm, "end": v(53.6, 65.6) * mm});
            skLineSegment(sketch, "E568", {"start": v(53.6, 65.6) * mm, "end": v(53.6, 54.4) * mm});
            skLineSegment(sketch, "E569", {"start": v(53.6, 54.4) * mm, "end": v(48.4, 54.4) * mm});
            skLineSegment(sketch, "E570", {"start": v(48.4, 54.4) * mm, "end": v(48.4, 65.6) * mm});
            skLineSegment(sketch, "E571", {"start": v(54.4, 65.6) * mm, "end": v(65.6, 65.6) * mm});
            skLineSegment(sketch, "E572", {"start": v(65.6, 65.6) * mm, "end": v(65.6, 60.4) * mm});
            skLineSegment(sketch, "E573", {"start": v(65.6, 60.4) * mm, "end": v(54.4, 60.4) * mm});
            skLineSegment(sketch, "E574", {"start": v(54.4, 60.4) * mm, "end": v(54.4, 65.6) * mm});
            skLineSegment(sketch, "E575", {"start": v(54.4, 59.6) * mm, "end": v(65.6, 59.6) * mm});
            skLineSegment(sketch, "E576", {"start": v(65.6, 59.6) * mm, "end": v(65.6, 54.4) * mm});
            skLineSegment(sketch, "E577", {"start": v(65.6, 54.4) * mm, "end": v(54.4, 54.4) * mm});
            skLineSegment(sketch, "E578", {"start": v(54.4, 54.4) * mm, "end": v(54.4, 59.6) * mm});
            skLineSegment(sketch, "E579", {"start": v(66.3, 65.59) * mm, "end": v(68.5, 65.59) * mm});
            skLineSegment(sketch, "E580", {"start": v(68.5, 65.59) * mm, "end": v(68.5, 60.39) * mm});
            skLineSegment(sketch, "E581", {"start": v(68.5, 60.39) * mm, "end": v(66.3, 60.39) * mm});
            skLineSegment(sketch, "E582", {"start": v(66.3, 60.39) * mm, "end": v(66.3, 65.59) * mm});
            skLineSegment(sketch, "E583", {"start": v(-74.6, 65.6) * mm, "end": v(-72.4, 65.6) * mm});
            skLineSegment(sketch, "E584", {"start": v(-72.4, 65.6) * mm, "end": v(-72.4, 60.4) * mm});
            skLineSegment(sketch, "E585", {"start": v(-72.4, 60.4) * mm, "end": v(-74.6, 60.4) * mm});
            skLineSegment(sketch, "E586", {"start": v(-74.6, 60.4) * mm, "end": v(-74.6, 65.6) * mm});
            skLineSegment(sketch, "E587", {"start": v(-74.6, 59.6) * mm, "end": v(-72.4, 59.6) * mm});
            skLineSegment(sketch, "E588", {"start": v(-72.4, 59.6) * mm, "end": v(-72.4, 54.4) * mm});
            skLineSegment(sketch, "E589", {"start": v(-72.4, 54.4) * mm, "end": v(-74.6, 54.4) * mm});
            skLineSegment(sketch, "E590", {"start": v(-74.6, 54.4) * mm, "end": v(-74.6, 59.6) * mm});
            skLineSegment(sketch, "E591", {"start": v(69.39, -48.46) * mm, "end": v(74.59, -48.46) * mm});
            skLineSegment(sketch, "E592", {"start": v(74.59, -48.46) * mm, "end": v(74.59, -59.65) * mm});
            skLineSegment(sketch, "E593", {"start": v(74.59, -59.65) * mm, "end": v(69.39, -59.65) * mm});
            skLineSegment(sketch, "E594", {"start": v(69.39, -59.65) * mm, "end": v(69.39, -48.46) * mm});
            skLineSegment(sketch, "E595", {"start": v(66.3, 59.56) * mm, "end": v(68.5, 59.56) * mm});
            skLineSegment(sketch, "E596", {"start": v(68.5, 59.56) * mm, "end": v(68.5, 54.36) * mm});
            skLineSegment(sketch, "E597", {"start": v(68.5, 54.36) * mm, "end": v(66.3, 54.36) * mm});
            skLineSegment(sketch, "E598", {"start": v(66.3, 54.36) * mm, "end": v(66.3, 59.56) * mm});
            skLineSegment(sketch, "E599", {"start": v(69.38, 57.27) * mm, "end": v(69.38, 59.47) * mm});
            skLineSegment(sketch, "E600", {"start": v(69.38, 59.47) * mm, "end": v(74.58, 59.47) * mm});
            skLineSegment(sketch, "E601", {"start": v(74.58, 59.47) * mm, "end": v(74.58, 57.27) * mm});
            skLineSegment(sketch, "E602", {"start": v(74.58, 57.27) * mm, "end": v(69.38, 57.27) * mm});
            skLineSegment(sketch, "E603", {"start": v(75.4, 57.27) * mm, "end": v(75.4, 59.47) * mm});
            skLineSegment(sketch, "E604", {"start": v(75.4, 59.47) * mm, "end": v(80.6, 59.47) * mm});
            skLineSegment(sketch, "E605", {"start": v(80.6, 59.47) * mm, "end": v(80.6, 57.27) * mm});
            skLineSegment(sketch, "E606", {"start": v(80.6, 57.27) * mm, "end": v(75.4, 57.27) * mm});
            skLineSegment(sketch, "E607.bottom", {"start": v(69.38, -47.88) * mm, "end": v(80.64, -47.88) * mm});
            skLineSegment(sketch, "E607.top", {"start": v(69.38, -45.1) * mm, "end": v(80.64, -45.1) * mm});
            skLineSegment(sketch, "E607.left", {"start": v(69.38, -47.88) * mm, "end": v(69.38, -45.1) * mm});
            skLineSegment(sketch, "E607.right", {"start": v(80.64, -47.88) * mm, "end": v(80.64, -45.1) * mm});
            skSolve(sketch);
        }
        {
            var Q0;
            Q0 = qSketchRegion(id + "F4", true);
            extrude(context, id + "F5", {"entities" : qUnion([Q0]), "operationType" : NewBodyOperationType.ADD, "depth" : 3.2 * mm, "offsetDistance" : 25 * mm});
        }
        {
            var Q0;
            Q0=makeQuery(id+"F5.opExtrude","CAP_FACE",FACE,{"disambiguationData":[OSD([sQuery(id+"F4.wireOp",EDGE,"E483"),sQuery(id+"F4.wireOp",EDGE,"E484"),sQuery(id+"F4.wireOp",EDGE,"E485"),sQuery(id+"F4.wireOp",EDGE,"E486")])],"isStart":false});
            var sketch = newSketch(context, id + "F6", { "sketchPlane" : qUnion([Q0])});
            skLineSegment(sketch, "E608.bottom", {"start": v(-79.98, 65.1) * mm, "end": v(70.1, 65.1) * mm});
            skLineSegment(sketch, "E608.top", {"start": v(-79.98, 55.07) * mm, "end": v(70.1, 55.07) * mm});
            skLineSegment(sketch, "E608.left", {"start": v(-79.98, 65.1) * mm, "end": v(-79.98, 55.07) * mm});
            skLineSegment(sketch, "E608.right", {"start": v(70.1, 65.1) * mm, "end": v(70.1, 55.07) * mm});
            skLineSegment(sketch, "E609.bottom", {"start": v(70.1, 65.1) * mm, "end": v(79.86, 65.1) * mm});
            skLineSegment(sketch, "E609.top", {"start": v(70.1, -64.92) * mm, "end": v(79.86, -64.92) * mm});
            skLineSegment(sketch, "E609.left", {"start": v(70.1, 65.1) * mm, "end": v(70.1, -64.92) * mm});
            skLineSegment(sketch, "E609.right", {"start": v(79.86, 65.1) * mm, "end": v(79.86, -64.92) * mm});
            skLineSegment(sketch, "E610.bottom", {"start": v(70.1, -64.92) * mm, "end": v(-80.1, -64.92) * mm});
            skLineSegment(sketch, "E610.top", {"start": v(70.1, -54.93) * mm, "end": v(-80.1, -54.93) * mm});
            skLineSegment(sketch, "E610.left", {"start": v(70.1, -64.92) * mm, "end": v(70.1, -54.93) * mm});
            skLineSegment(sketch, "E610.right", {"start": v(-80.1, -64.92) * mm, "end": v(-80.1, -54.93) * mm});
            skSolve(sketch);
        }
        {
            var Q0;
            Q0=makeQuery(id+"F6.imprint","IMPRINT",FACE,{"disambiguationData":[TD([[makeQuery(id+"F6.imprint","IMPRINT",EDGE,{"derivedFrom":sQuery(id+"F6.wireOp",EDGE,"E610.bottom")}),-1.0]])]});
            var Q1;
            Q1 = qSketchRegion(id + "F6", true);
            extrude(context, id + "F7", {"entities" : qUnion([Q0, Q1]), "depth" : .8 * mm, "offsetDistance" : 25 * mm, "hasSecondDirection" : true, "secondDirectionOppositeDirection" : true, "secondDirectionDepth" : 4 * mm});
        }
        {
            var Q0;
            Q0=makeQuery(id+"F7.opExtrude","CAP_FACE",FACE,{"disambiguationData":[OSD([sQuery(id+"F6.wireOp",EDGE,"E608.bottom"),sQuery(id+"F6.wireOp",EDGE,"E608.top"),sQuery(id+"F6.wireOp",EDGE,"E608.left"),sQuery(id+"F6.wireOp",EDGE,"E609.bottom"),sQuery(id+"F6.wireOp",EDGE,"E609.top"),sQuery(id+"F6.wireOp",EDGE,"E609.left"),sQuery(id+"F6.wireOp",EDGE,"E609.right"),sQuery(id+"F6.wireOp",EDGE,"E610.bottom"),sQuery(id+"F6.wireOp",EDGE,"E610.top"),sQuery(id+"F6.wireOp",EDGE,"E610.right")])],"isStart":false});
            var sketch = newSketch(context, id + "F8", { "sketchPlane" : qUnion([Q0])});
            skLineSegment(sketch, "E611.bottom", {"start": v(-80.83, 65.93) * mm, "end": v(82.25, 65.93) * mm});
            skLineSegment(sketch, "E611.top", {"start": v(-80.83, -54.38) * mm, "end": v(82.25, -54.38) * mm});
            skLineSegment(sketch, "E611.left", {"start": v(-80.83, 65.93) * mm, "end": v(-80.83, -54.38) * mm});
            skLineSegment(sketch, "E611.right", {"start": v(82.25, 65.93) * mm, "end": v(82.25, -54.38) * mm});
            skSolve(sketch);
        }
        {
            var Q0;
            Q0=makeQuery(id+"F8.imprint","IMPRINT",FACE,{"disambiguationData":[TD([[makeQuery(id+"F8.imprint","IMPRINT",EDGE,{"derivedFrom":sQuery(id+"F8.wireOp",EDGE,"E611.bottom")}),-1.0]])]});
            var Q1;
            {var subQ1=makeQuery(id+"F7.opExtrude","CAP_EDGE",EDGE,{"disambiguationData":[OSD([sQuery(id+"F6.wireOp",EDGE,"E608.top")])],"isStart":false});Q1=makeQuery(id+"F8.imprint","IMPRINT",FACE,{"disambiguationData":[TD([[makeQuery(id+"F8.imprint","IMPRINT",EDGE,{"derivedFrom":subQ1}),1.0]])]});}
            extrude(context, id + "F9", {"entities" : qUnion([Q0, Q1]), "operationType" : NewBodyOperationType.REMOVE, "oppositeDirection" : true, "depth" : 25 * mm, "offsetDistance" : 25 * mm});
        }
    });
